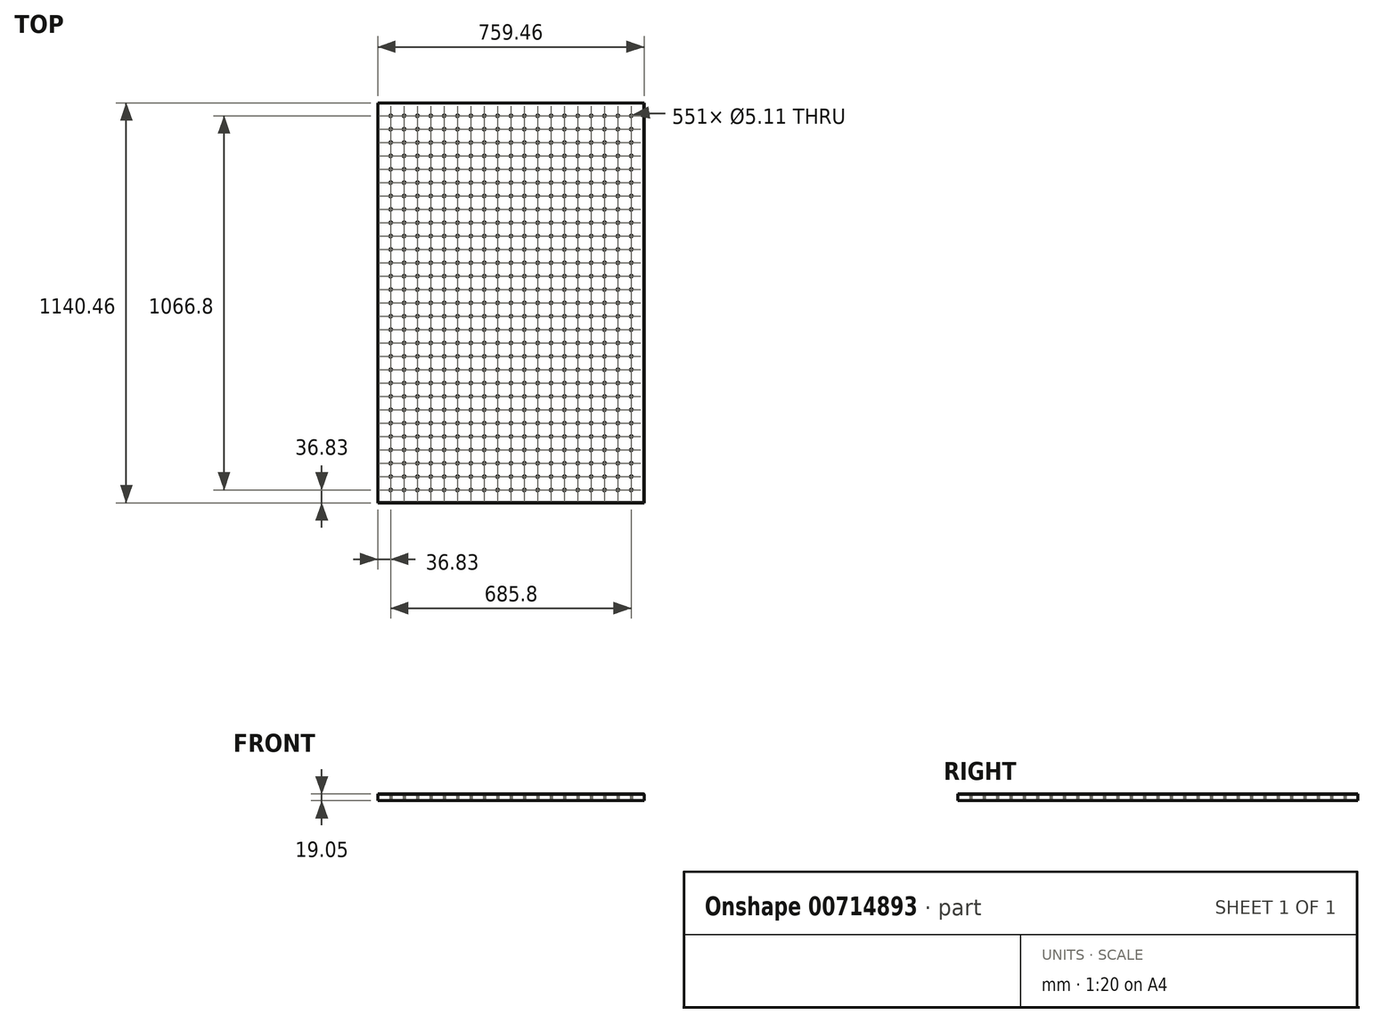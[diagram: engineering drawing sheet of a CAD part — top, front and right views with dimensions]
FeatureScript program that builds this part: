
annotation { "Feature Type Name" : "Feature", "Feature Type Description" : "" }
export const myFeature = defineFeature(function(context is Context, id is Id, definition is map)
    precondition{}
    {
        {
            var Q0;
            Q0=qCreatedBy(makeId("Top.planeOp"),FACE);
            var sketch = newSketch(context, id + "F0", { "sketchPlane" : qUnion([Q0])});
            skLineSegment(sketch, "E0.bottom", {"start": v(379.73, 570.23) * mm, "end": v(-379.73, 570.23) * mm});
            skLineSegment(sketch, "E0.top", {"start": v(379.73, -570.23) * mm, "end": v(-379.73, -570.23) * mm});
            skLineSegment(sketch, "E0.left", {"start": v(379.73, 570.23) * mm, "end": v(379.73, -570.23) * mm});
            skLineSegment(sketch, "E0.right", {"start": v(-379.73, 570.23) * mm, "end": v(-379.73, -570.23) * mm});
            skPoint(sketch, "E0.middle", {"position": v(0, 0) * mm});
            skLineSegment(sketch, "E1", {"start": v(0, 570.23) * mm, "end": v(0, -570.23) * mm, "construction": true});
            skCircle(sketch, "E2", {"center": v(0, 0) * mm, "radius": 2.55 * mm});
            skCircle(sketch, "E3.0.1.0", {"center": v(0, 38.1) * mm, "radius": 2.55 * mm});
            skCircle(sketch, "E3.0.2.0", {"center": v(0, 76.2) * mm, "radius": 2.55 * mm});
            skCircle(sketch, "E3.0.3.0", {"center": v(0, 114.3) * mm, "radius": 2.55 * mm});
            skCircle(sketch, "E3.0.4.0", {"center": v(0, 152.4) * mm, "radius": 2.55 * mm});
            skCircle(sketch, "E3.0.5.0", {"center": v(0, 190.5) * mm, "radius": 2.55 * mm});
            skCircle(sketch, "E3.0.6.0", {"center": v(0, 228.6) * mm, "radius": 2.55 * mm});
            skCircle(sketch, "E3.0.7.0", {"center": v(0, 266.7) * mm, "radius": 2.55 * mm});
            skCircle(sketch, "E3.0.8.0", {"center": v(0, 304.8) * mm, "radius": 2.55 * mm});
            skCircle(sketch, "E3.0.9.0", {"center": v(0, 342.9) * mm, "radius": 2.55 * mm});
            skCircle(sketch, "E3.0.10.0", {"center": v(0, 381) * mm, "radius": 2.55 * mm});
            skCircle(sketch, "E3.1.0.0", {"center": v(38.1, 0) * mm, "radius": 2.55 * mm});
            skCircle(sketch, "E3.1.1.0", {"center": v(38.1, 38.1) * mm, "radius": 2.55 * mm});
            skCircle(sketch, "E3.1.2.0", {"center": v(38.1, 76.2) * mm, "radius": 2.55 * mm});
            skCircle(sketch, "E3.1.3.0", {"center": v(38.1, 114.3) * mm, "radius": 2.55 * mm});
            skCircle(sketch, "E3.1.4.0", {"center": v(38.1, 152.4) * mm, "radius": 2.55 * mm});
            skCircle(sketch, "E3.1.5.0", {"center": v(38.1, 190.5) * mm, "radius": 2.55 * mm});
            skCircle(sketch, "E3.1.6.0", {"center": v(38.1, 228.6) * mm, "radius": 2.55 * mm});
            skCircle(sketch, "E3.1.7.0", {"center": v(38.1, 266.7) * mm, "radius": 2.55 * mm});
            skCircle(sketch, "E3.1.8.0", {"center": v(38.1, 304.8) * mm, "radius": 2.55 * mm});
            skCircle(sketch, "E3.1.9.0", {"center": v(38.1, 342.9) * mm, "radius": 2.55 * mm});
            skCircle(sketch, "E3.1.10.0", {"center": v(38.1, 381) * mm, "radius": 2.55 * mm});
            skCircle(sketch, "E3.2.0.0", {"center": v(76.2, 0) * mm, "radius": 2.55 * mm});
            skCircle(sketch, "E3.2.1.0", {"center": v(76.2, 38.1) * mm, "radius": 2.55 * mm});
            skCircle(sketch, "E3.2.2.0", {"center": v(76.2, 76.2) * mm, "radius": 2.55 * mm});
            skCircle(sketch, "E3.2.3.0", {"center": v(76.2, 114.3) * mm, "radius": 2.55 * mm});
            skCircle(sketch, "E3.2.4.0", {"center": v(76.2, 152.4) * mm, "radius": 2.55 * mm});
            skCircle(sketch, "E3.2.5.0", {"center": v(76.2, 190.5) * mm, "radius": 2.55 * mm});
            skCircle(sketch, "E3.2.6.0", {"center": v(76.2, 228.6) * mm, "radius": 2.55 * mm});
            skCircle(sketch, "E3.2.7.0", {"center": v(76.2, 266.7) * mm, "radius": 2.55 * mm});
            skCircle(sketch, "E3.2.8.0", {"center": v(76.2, 304.8) * mm, "radius": 2.55 * mm});
            skCircle(sketch, "E3.2.9.0", {"center": v(76.2, 342.9) * mm, "radius": 2.55 * mm});
            skCircle(sketch, "E3.2.10.0", {"center": v(76.2, 381) * mm, "radius": 2.55 * mm});
            skCircle(sketch, "E3.3.0.0", {"center": v(114.3, 0) * mm, "radius": 2.55 * mm});
            skCircle(sketch, "E3.3.1.0", {"center": v(114.3, 38.1) * mm, "radius": 2.55 * mm});
            skCircle(sketch, "E3.3.2.0", {"center": v(114.3, 76.2) * mm, "radius": 2.55 * mm});
            skCircle(sketch, "E3.3.3.0", {"center": v(114.3, 114.3) * mm, "radius": 2.55 * mm});
            skCircle(sketch, "E3.3.4.0", {"center": v(114.3, 152.4) * mm, "radius": 2.55 * mm});
            skCircle(sketch, "E3.3.5.0", {"center": v(114.3, 190.5) * mm, "radius": 2.55 * mm});
            skCircle(sketch, "E3.3.6.0", {"center": v(114.3, 228.6) * mm, "radius": 2.55 * mm});
            skCircle(sketch, "E3.3.7.0", {"center": v(114.3, 266.7) * mm, "radius": 2.55 * mm});
            skCircle(sketch, "E3.3.8.0", {"center": v(114.3, 304.8) * mm, "radius": 2.55 * mm});
            skCircle(sketch, "E3.3.9.0", {"center": v(114.3, 342.9) * mm, "radius": 2.55 * mm});
            skCircle(sketch, "E3.3.10.0", {"center": v(114.3, 381) * mm, "radius": 2.55 * mm});
            skCircle(sketch, "E3.4.0.0", {"center": v(152.4, 0) * mm, "radius": 2.55 * mm});
            skCircle(sketch, "E3.4.1.0", {"center": v(152.4, 38.1) * mm, "radius": 2.55 * mm});
            skCircle(sketch, "E3.4.2.0", {"center": v(152.4, 76.2) * mm, "radius": 2.55 * mm});
            skCircle(sketch, "E3.4.3.0", {"center": v(152.4, 114.3) * mm, "radius": 2.55 * mm});
            skCircle(sketch, "E3.4.4.0", {"center": v(152.4, 152.4) * mm, "radius": 2.55 * mm});
            skCircle(sketch, "E3.4.5.0", {"center": v(152.4, 190.5) * mm, "radius": 2.55 * mm});
            skCircle(sketch, "E3.4.6.0", {"center": v(152.4, 228.6) * mm, "radius": 2.55 * mm});
            skCircle(sketch, "E3.4.7.0", {"center": v(152.4, 266.7) * mm, "radius": 2.55 * mm});
            skCircle(sketch, "E3.4.8.0", {"center": v(152.4, 304.8) * mm, "radius": 2.55 * mm});
            skCircle(sketch, "E3.4.9.0", {"center": v(152.4, 342.9) * mm, "radius": 2.55 * mm});
            skCircle(sketch, "E3.4.10.0", {"center": v(152.4, 381) * mm, "radius": 2.55 * mm});
            skCircle(sketch, "E3.5.0.0", {"center": v(190.5, 0) * mm, "radius": 2.55 * mm});
            skCircle(sketch, "E3.5.1.0", {"center": v(190.5, 38.1) * mm, "radius": 2.55 * mm});
            skCircle(sketch, "E3.5.2.0", {"center": v(190.5, 76.2) * mm, "radius": 2.55 * mm});
            skCircle(sketch, "E3.5.3.0", {"center": v(190.5, 114.3) * mm, "radius": 2.55 * mm});
            skCircle(sketch, "E3.5.4.0", {"center": v(190.5, 152.4) * mm, "radius": 2.55 * mm});
            skCircle(sketch, "E3.5.5.0", {"center": v(190.5, 190.5) * mm, "radius": 2.55 * mm});
            skCircle(sketch, "E3.5.6.0", {"center": v(190.5, 228.6) * mm, "radius": 2.55 * mm});
            skCircle(sketch, "E3.5.7.0", {"center": v(190.5, 266.7) * mm, "radius": 2.55 * mm});
            skCircle(sketch, "E3.5.8.0", {"center": v(190.5, 304.8) * mm, "radius": 2.55 * mm});
            skCircle(sketch, "E3.5.9.0", {"center": v(190.5, 342.9) * mm, "radius": 2.55 * mm});
            skCircle(sketch, "E3.5.10.0", {"center": v(190.5, 381) * mm, "radius": 2.55 * mm});
            skCircle(sketch, "E3.6.0.0", {"center": v(228.6, 0) * mm, "radius": 2.55 * mm});
            skCircle(sketch, "E3.6.1.0", {"center": v(228.6, 38.1) * mm, "radius": 2.55 * mm});
            skCircle(sketch, "E3.6.2.0", {"center": v(228.6, 76.2) * mm, "radius": 2.55 * mm});
            skCircle(sketch, "E3.6.3.0", {"center": v(228.6, 114.3) * mm, "radius": 2.55 * mm});
            skCircle(sketch, "E3.6.4.0", {"center": v(228.6, 152.4) * mm, "radius": 2.55 * mm});
            skCircle(sketch, "E3.6.5.0", {"center": v(228.6, 190.5) * mm, "radius": 2.55 * mm});
            skCircle(sketch, "E3.6.6.0", {"center": v(228.6, 228.6) * mm, "radius": 2.55 * mm});
            skCircle(sketch, "E3.6.7.0", {"center": v(228.6, 266.7) * mm, "radius": 2.55 * mm});
            skCircle(sketch, "E3.6.8.0", {"center": v(228.6, 304.8) * mm, "radius": 2.55 * mm});
            skCircle(sketch, "E3.6.9.0", {"center": v(228.6, 342.9) * mm, "radius": 2.55 * mm});
            skCircle(sketch, "E3.6.10.0", {"center": v(228.6, 381) * mm, "radius": 2.55 * mm});
            skCircle(sketch, "E3.7.0.0", {"center": v(266.7, 0) * mm, "radius": 2.55 * mm});
            skCircle(sketch, "E3.7.1.0", {"center": v(266.7, 38.1) * mm, "radius": 2.55 * mm});
            skCircle(sketch, "E3.7.2.0", {"center": v(266.7, 76.2) * mm, "radius": 2.55 * mm});
            skCircle(sketch, "E3.7.3.0", {"center": v(266.7, 114.3) * mm, "radius": 2.55 * mm});
            skCircle(sketch, "E3.7.4.0", {"center": v(266.7, 152.4) * mm, "radius": 2.55 * mm});
            skCircle(sketch, "E3.7.5.0", {"center": v(266.7, 190.5) * mm, "radius": 2.55 * mm});
            skCircle(sketch, "E3.7.6.0", {"center": v(266.7, 228.6) * mm, "radius": 2.55 * mm});
            skCircle(sketch, "E3.7.7.0", {"center": v(266.7, 266.7) * mm, "radius": 2.55 * mm});
            skCircle(sketch, "E3.7.8.0", {"center": v(266.7, 304.8) * mm, "radius": 2.55 * mm});
            skCircle(sketch, "E3.7.9.0", {"center": v(266.7, 342.9) * mm, "radius": 2.55 * mm});
            skCircle(sketch, "E3.7.10.0", {"center": v(266.7, 381) * mm, "radius": 2.55 * mm});
            skLineSegment(sketch, "E3.direction1", {"start": v(0, 0) * mm, "end": v(38.1, 0) * mm, "construction": true});
            skLineSegment(sketch, "E3.direction2", {"start": v(0, 0) * mm, "end": v(0, 38.1) * mm, "construction": true});
            skCircle(sketch, "E4.0.0.11", {"center": v(0, 419.1) * mm, "radius": 2.55 * mm});
            skCircle(sketch, "E4.0.1.11", {"center": v(38.1, 419.1) * mm, "radius": 2.55 * mm});
            skCircle(sketch, "E4.0.2.11", {"center": v(76.2, 419.1) * mm, "radius": 2.55 * mm});
            skCircle(sketch, "E4.0.3.11", {"center": v(114.3, 419.1) * mm, "radius": 2.55 * mm});
            skCircle(sketch, "E4.0.4.11", {"center": v(152.4, 419.1) * mm, "radius": 2.55 * mm});
            skCircle(sketch, "E4.0.5.11", {"center": v(190.5, 419.1) * mm, "radius": 2.55 * mm});
            skCircle(sketch, "E4.0.6.11", {"center": v(228.6, 419.1) * mm, "radius": 2.55 * mm});
            skCircle(sketch, "E4.0.7.11", {"center": v(266.7, 419.1) * mm, "radius": 2.55 * mm});
            skCircle(sketch, "E5.0.0.12", {"center": v(0, 457.2) * mm, "radius": 2.55 * mm});
            skCircle(sketch, "E5.0.0.13", {"center": v(0, 495.3) * mm, "radius": 2.55 * mm});
            skCircle(sketch, "E5.0.0.14", {"center": v(0, 533.4) * mm, "radius": 2.55 * mm});
            skCircle(sketch, "E5.0.1.12", {"center": v(38.1, 457.2) * mm, "radius": 2.55 * mm});
            skCircle(sketch, "E5.0.1.13", {"center": v(38.1, 495.3) * mm, "radius": 2.55 * mm});
            skCircle(sketch, "E5.0.1.14", {"center": v(38.1, 533.4) * mm, "radius": 2.55 * mm});
            skCircle(sketch, "E5.0.2.12", {"center": v(76.2, 457.2) * mm, "radius": 2.55 * mm});
            skCircle(sketch, "E5.0.2.13", {"center": v(76.2, 495.3) * mm, "radius": 2.55 * mm});
            skCircle(sketch, "E5.0.2.14", {"center": v(76.2, 533.4) * mm, "radius": 2.55 * mm});
            skCircle(sketch, "E5.0.3.12", {"center": v(114.3, 457.2) * mm, "radius": 2.55 * mm});
            skCircle(sketch, "E5.0.3.13", {"center": v(114.3, 495.3) * mm, "radius": 2.55 * mm});
            skCircle(sketch, "E5.0.3.14", {"center": v(114.3, 533.4) * mm, "radius": 2.55 * mm});
            skCircle(sketch, "E5.0.4.12", {"center": v(152.4, 457.2) * mm, "radius": 2.55 * mm});
            skCircle(sketch, "E5.0.4.13", {"center": v(152.4, 495.3) * mm, "radius": 2.55 * mm});
            skCircle(sketch, "E5.0.4.14", {"center": v(152.4, 533.4) * mm, "radius": 2.55 * mm});
            skCircle(sketch, "E5.0.5.12", {"center": v(190.5, 457.2) * mm, "radius": 2.55 * mm});
            skCircle(sketch, "E5.0.5.13", {"center": v(190.5, 495.3) * mm, "radius": 2.55 * mm});
            skCircle(sketch, "E5.0.5.14", {"center": v(190.5, 533.4) * mm, "radius": 2.55 * mm});
            skCircle(sketch, "E5.0.6.12", {"center": v(228.6, 457.2) * mm, "radius": 2.55 * mm});
            skCircle(sketch, "E5.0.6.13", {"center": v(228.6, 495.3) * mm, "radius": 2.55 * mm});
            skCircle(sketch, "E5.0.6.14", {"center": v(228.6, 533.4) * mm, "radius": 2.55 * mm});
            skCircle(sketch, "E5.0.7.12", {"center": v(266.7, 457.2) * mm, "radius": 2.55 * mm});
            skCircle(sketch, "E5.0.7.13", {"center": v(266.7, 495.3) * mm, "radius": 2.55 * mm});
            skCircle(sketch, "E5.0.7.14", {"center": v(266.7, 533.4) * mm, "radius": 2.55 * mm});
            skCircle(sketch, "E6.0.8.0", {"center": v(304.8, 0) * mm, "radius": 2.55 * mm});
            skCircle(sketch, "E6.0.8.1", {"center": v(304.8, 38.1) * mm, "radius": 2.55 * mm});
            skCircle(sketch, "E6.0.8.2", {"center": v(304.8, 76.2) * mm, "radius": 2.55 * mm});
            skCircle(sketch, "E6.0.8.3", {"center": v(304.8, 114.3) * mm, "radius": 2.55 * mm});
            skCircle(sketch, "E6.0.8.4", {"center": v(304.8, 152.4) * mm, "radius": 2.55 * mm});
            skCircle(sketch, "E6.0.8.5", {"center": v(304.8, 190.5) * mm, "radius": 2.55 * mm});
            skCircle(sketch, "E6.0.8.6", {"center": v(304.8, 228.6) * mm, "radius": 2.55 * mm});
            skCircle(sketch, "E6.0.8.7", {"center": v(304.8, 266.7) * mm, "radius": 2.55 * mm});
            skCircle(sketch, "E6.0.8.8", {"center": v(304.8, 304.8) * mm, "radius": 2.55 * mm});
            skCircle(sketch, "E6.0.8.9", {"center": v(304.8, 342.9) * mm, "radius": 2.55 * mm});
            skCircle(sketch, "E6.0.8.10", {"center": v(304.8, 381) * mm, "radius": 2.55 * mm});
            skCircle(sketch, "E6.0.8.11", {"center": v(304.8, 419.1) * mm, "radius": 2.55 * mm});
            skCircle(sketch, "E6.0.8.12", {"center": v(304.8, 457.2) * mm, "radius": 2.55 * mm});
            skCircle(sketch, "E6.0.8.13", {"center": v(304.8, 495.3) * mm, "radius": 2.55 * mm});
            skCircle(sketch, "E6.0.8.14", {"center": v(304.8, 533.4) * mm, "radius": 2.55 * mm});
            skCircle(sketch, "E6.0.9.0", {"center": v(342.9, 0) * mm, "radius": 2.55 * mm});
            skCircle(sketch, "E6.0.9.1", {"center": v(342.9, 38.1) * mm, "radius": 2.55 * mm});
            skCircle(sketch, "E6.0.9.2", {"center": v(342.9, 76.2) * mm, "radius": 2.55 * mm});
            skCircle(sketch, "E6.0.9.3", {"center": v(342.9, 114.3) * mm, "radius": 2.55 * mm});
            skCircle(sketch, "E6.0.9.4", {"center": v(342.9, 152.4) * mm, "radius": 2.55 * mm});
            skCircle(sketch, "E6.0.9.5", {"center": v(342.9, 190.5) * mm, "radius": 2.55 * mm});
            skCircle(sketch, "E6.0.9.6", {"center": v(342.9, 228.6) * mm, "radius": 2.55 * mm});
            skCircle(sketch, "E6.0.9.7", {"center": v(342.9, 266.7) * mm, "radius": 2.55 * mm});
            skCircle(sketch, "E6.0.9.8", {"center": v(342.9, 304.8) * mm, "radius": 2.55 * mm});
            skCircle(sketch, "E6.0.9.9", {"center": v(342.9, 342.9) * mm, "radius": 2.55 * mm});
            skCircle(sketch, "E6.0.9.10", {"center": v(342.9, 381) * mm, "radius": 2.55 * mm});
            skCircle(sketch, "E6.0.9.11", {"center": v(342.9, 419.1) * mm, "radius": 2.55 * mm});
            skCircle(sketch, "E6.0.9.12", {"center": v(342.9, 457.2) * mm, "radius": 2.55 * mm});
            skCircle(sketch, "E6.0.9.13", {"center": v(342.9, 495.3) * mm, "radius": 2.55 * mm});
            skCircle(sketch, "E6.0.9.14", {"center": v(342.9, 533.4) * mm, "radius": 2.55 * mm});
            skLineSegment(sketch, "E7", {"start": v(-379.73, 0) * mm, "end": v(379.73, 0) * mm, "construction": true});
            skCircle(sketch, "E8.MirrorC", {"center": v(-228.6, 495.3) * mm, "radius": 2.55 * mm});
            skCircle(sketch, "E9.MirrorC", {"center": v(-76.2, 457.2) * mm, "radius": 2.55 * mm});
            skCircle(sketch, "E10.MirrorC", {"center": v(-266.7, 495.3) * mm, "radius": 2.55 * mm});
            skCircle(sketch, "E11.MirrorC", {"center": v(-114.3, 190.5) * mm, "radius": 2.55 * mm});
            skCircle(sketch, "E12.MirrorC", {"center": v(-304.8, 38.1) * mm, "radius": 2.55 * mm});
            skCircle(sketch, "E13.MirrorC", {"center": v(-114.3, 457.2) * mm, "radius": 2.55 * mm});
            skCircle(sketch, "E14.MirrorC", {"center": v(-266.7, 342.9) * mm, "radius": 2.55 * mm});
            skCircle(sketch, "E15.MirrorC", {"center": v(-304.8, 114.3) * mm, "radius": 2.55 * mm});
            skCircle(sketch, "E16.MirrorC", {"center": v(-76.2, 114.3) * mm, "radius": 2.55 * mm});
            skCircle(sketch, "E17.MirrorC", {"center": v(-190.5, 38.1) * mm, "radius": 2.55 * mm});
            skCircle(sketch, "E18.MirrorC", {"center": v(-190.5, 342.9) * mm, "radius": 2.55 * mm});
            skCircle(sketch, "E19.MirrorC", {"center": v(-266.7, 114.3) * mm, "radius": 2.55 * mm});
            skCircle(sketch, "E20.MirrorC", {"center": v(-266.7, 304.8) * mm, "radius": 2.55 * mm});
            skCircle(sketch, "E21.MirrorC", {"center": v(-190.5, 152.4) * mm, "radius": 2.55 * mm});
            skCircle(sketch, "E22.MirrorC", {"center": v(-38.1, 457.2) * mm, "radius": 2.55 * mm});
            skCircle(sketch, "E23.MirrorC", {"center": v(-228.6, 114.3) * mm, "radius": 2.55 * mm});
            skCircle(sketch, "E24.MirrorC", {"center": v(-342.9, 457.2) * mm, "radius": 2.55 * mm});
            skCircle(sketch, "E25.MirrorC", {"center": v(-76.2, 266.7) * mm, "radius": 2.55 * mm});
            skCircle(sketch, "E26.MirrorC", {"center": v(-228.6, 152.4) * mm, "radius": 2.55 * mm});
            skCircle(sketch, "E27.MirrorC", {"center": v(-38.1, 419.1) * mm, "radius": 2.55 * mm});
            skCircle(sketch, "E28.MirrorC", {"center": v(-38.1, 381) * mm, "radius": 2.55 * mm});
            skCircle(sketch, "E29.MirrorC", {"center": v(-114.3, 152.4) * mm, "radius": 2.55 * mm});
            skCircle(sketch, "E30.MirrorC", {"center": v(-228.6, 76.2) * mm, "radius": 2.55 * mm});
            skCircle(sketch, "E31.MirrorC", {"center": v(-266.7, 266.7) * mm, "radius": 2.55 * mm});
            skCircle(sketch, "E32.MirrorC", {"center": v(-38.1, 342.9) * mm, "radius": 2.55 * mm});
            skCircle(sketch, "E33.MirrorC", {"center": v(-152.4, 304.8) * mm, "radius": 2.55 * mm});
            skCircle(sketch, "E34.MirrorC", {"center": v(-342.9, 38.1) * mm, "radius": 2.55 * mm});
            skCircle(sketch, "E35.MirrorC", {"center": v(-114.3, 266.7) * mm, "radius": 2.55 * mm});
            skCircle(sketch, "E36.MirrorC", {"center": v(-76.2, 152.4) * mm, "radius": 2.55 * mm});
            skCircle(sketch, "E37.MirrorC", {"center": v(-228.6, 304.8) * mm, "radius": 2.55 * mm});
            skCircle(sketch, "E38.MirrorC", {"center": v(-38.1, 190.5) * mm, "radius": 2.55 * mm});
            skCircle(sketch, "E39.MirrorC", {"center": v(-114.3, 38.1) * mm, "radius": 2.55 * mm});
            skCircle(sketch, "E40.MirrorC", {"center": v(-152.4, 228.6) * mm, "radius": 2.55 * mm});
            skCircle(sketch, "E41.MirrorC", {"center": v(-266.7, 152.4) * mm, "radius": 2.55 * mm});
            skCircle(sketch, "E42.MirrorC", {"center": v(-266.7, 533.4) * mm, "radius": 2.55 * mm});
            skCircle(sketch, "E43.MirrorC", {"center": v(-228.6, 533.4) * mm, "radius": 2.55 * mm});
            skCircle(sketch, "E44.MirrorC", {"center": v(-76.2, 381) * mm, "radius": 2.55 * mm});
            skCircle(sketch, "E45.MirrorC", {"center": v(-114.3, 533.4) * mm, "radius": 2.55 * mm});
            skCircle(sketch, "E46.MirrorC", {"center": v(-114.3, 495.3) * mm, "radius": 2.55 * mm});
            skCircle(sketch, "E47.MirrorC", {"center": v(-342.9, 114.3) * mm, "radius": 2.55 * mm});
            skCircle(sketch, "E48.MirrorC", {"center": v(-152.4, 381) * mm, "radius": 2.55 * mm});
            skCircle(sketch, "E49.MirrorC", {"center": v(-228.6, 419.1) * mm, "radius": 2.55 * mm});
            skCircle(sketch, "E50.MirrorC", {"center": v(-304.8, 342.9) * mm, "radius": 2.55 * mm});
            skCircle(sketch, "E51.MirrorC", {"center": v(-114.3, 304.8) * mm, "radius": 2.55 * mm});
            skCircle(sketch, "E52.MirrorC", {"center": v(-342.9, 228.6) * mm, "radius": 2.55 * mm});
            skCircle(sketch, "E53.MirrorC", {"center": v(-76.2, 342.9) * mm, "radius": 2.55 * mm});
            skCircle(sketch, "E54.MirrorC", {"center": v(-342.9, 152.4) * mm, "radius": 2.55 * mm});
            skCircle(sketch, "E55.MirrorC", {"center": v(-190.5, 76.2) * mm, "radius": 2.55 * mm});
            skCircle(sketch, "E56.MirrorC", {"center": v(-228.6, 38.1) * mm, "radius": 2.55 * mm});
            skCircle(sketch, "E57.MirrorC", {"center": v(-152.4, 114.3) * mm, "radius": 2.55 * mm});
            skCircle(sketch, "E58.MirrorC", {"center": v(-38.1, 304.8) * mm, "radius": 2.55 * mm});
            skCircle(sketch, "E59.MirrorC", {"center": v(-152.4, 266.7) * mm, "radius": 2.55 * mm});
            skCircle(sketch, "E60.MirrorC", {"center": v(-190.5, 304.8) * mm, "radius": 2.55 * mm});
            skCircle(sketch, "E61.MirrorC", {"center": v(-266.7, 76.2) * mm, "radius": 2.55 * mm});
            skCircle(sketch, "E62.MirrorC", {"center": v(-114.3, 76.2) * mm, "radius": 2.55 * mm});
            skCircle(sketch, "E63.MirrorC", {"center": v(-304.8, 304.8) * mm, "radius": 2.55 * mm});
            skCircle(sketch, "E64.MirrorC", {"center": v(-304.8, 533.4) * mm, "radius": 2.55 * mm});
            skCircle(sketch, "E65.MirrorC", {"center": v(-190.5, 114.3) * mm, "radius": 2.55 * mm});
            skCircle(sketch, "E66.MirrorC", {"center": v(-76.2, 76.2) * mm, "radius": 2.55 * mm});
            skCircle(sketch, "E67.MirrorC", {"center": v(-266.7, 190.5) * mm, "radius": 2.55 * mm});
            skCircle(sketch, "E68.MirrorC", {"center": v(-152.4, 38.1) * mm, "radius": 2.55 * mm});
            skCircle(sketch, "E69.MirrorC", {"center": v(-190.5, 228.6) * mm, "radius": 2.55 * mm});
            skCircle(sketch, "E70.MirrorC", {"center": v(-190.5, 495.3) * mm, "radius": 2.55 * mm});
            skCircle(sketch, "E71.MirrorC", {"center": v(-38.1, 266.7) * mm, "radius": 2.55 * mm});
            skCircle(sketch, "E72.MirrorC", {"center": v(-152.4, 495.3) * mm, "radius": 2.55 * mm});
            skCircle(sketch, "E73.MirrorC", {"center": v(-38.1, 152.4) * mm, "radius": 2.55 * mm});
            skCircle(sketch, "E74.MirrorC", {"center": v(-304.8, 495.3) * mm, "radius": 2.55 * mm});
            skCircle(sketch, "E75.MirrorC", {"center": v(-304.8, 381) * mm, "radius": 2.55 * mm});
            skCircle(sketch, "E76.MirrorC", {"center": v(-228.6, 190.5) * mm, "radius": 2.55 * mm});
            skCircle(sketch, "E77.MirrorC", {"center": v(-38.1, 76.2) * mm, "radius": 2.55 * mm});
            skCircle(sketch, "E78.MirrorC", {"center": v(-342.9, 76.2) * mm, "radius": 2.55 * mm});
            skCircle(sketch, "E79.MirrorC", {"center": v(-266.7, 419.1) * mm, "radius": 2.55 * mm});
            skCircle(sketch, "E80.MirrorC", {"center": v(-190.5, 190.5) * mm, "radius": 2.55 * mm});
            skCircle(sketch, "E81.MirrorC", {"center": v(-152.4, 419.1) * mm, "radius": 2.55 * mm});
            skCircle(sketch, "E82.MirrorC", {"center": v(-38.1, 533.4) * mm, "radius": 2.55 * mm});
            skCircle(sketch, "E83.MirrorC", {"center": v(-76.2, 228.6) * mm, "radius": 2.55 * mm});
            skCircle(sketch, "E84.MirrorC", {"center": v(-114.3, 342.9) * mm, "radius": 2.55 * mm});
            skCircle(sketch, "E85.MirrorC", {"center": v(-228.6, 266.7) * mm, "radius": 2.55 * mm});
            skCircle(sketch, "E86.MirrorC", {"center": v(-304.8, 419.1) * mm, "radius": 2.55 * mm});
            skCircle(sketch, "E87.MirrorC", {"center": v(-38.1, 495.3) * mm, "radius": 2.55 * mm});
            skCircle(sketch, "E88.MirrorC", {"center": v(-190.5, 381) * mm, "radius": 2.55 * mm});
            skCircle(sketch, "E89.MirrorC", {"center": v(-304.8, 76.2) * mm, "radius": 2.55 * mm});
            skCircle(sketch, "E90.MirrorC", {"center": v(-190.5, 457.2) * mm, "radius": 2.55 * mm});
            skCircle(sketch, "E91.MirrorC", {"center": v(-76.2, 419.1) * mm, "radius": 2.55 * mm});
            skCircle(sketch, "E92.MirrorC", {"center": v(-342.9, 266.7) * mm, "radius": 2.55 * mm});
            skCircle(sketch, "E93.MirrorC", {"center": v(-190.5, 533.4) * mm, "radius": 2.55 * mm});
            skCircle(sketch, "E94.MirrorC", {"center": v(-266.7, 228.6) * mm, "radius": 2.55 * mm});
            skCircle(sketch, "E95.MirrorC", {"center": v(-342.9, 381) * mm, "radius": 2.55 * mm});
            skCircle(sketch, "E96.MirrorC", {"center": v(-38.1, 38.1) * mm, "radius": 2.55 * mm});
            skCircle(sketch, "E97.MirrorC", {"center": v(-114.3, 228.6) * mm, "radius": 2.55 * mm});
            skCircle(sketch, "E98.MirrorC", {"center": v(-38.1, 228.6) * mm, "radius": 2.55 * mm});
            skCircle(sketch, "E99.MirrorC", {"center": v(-304.8, 190.5) * mm, "radius": 2.55 * mm});
            skCircle(sketch, "E100.MirrorC", {"center": v(-114.3, 114.3) * mm, "radius": 2.55 * mm});
            skCircle(sketch, "E101.MirrorC", {"center": v(-228.6, 457.2) * mm, "radius": 2.55 * mm});
            skCircle(sketch, "E102.MirrorC", {"center": v(-342.9, 419.1) * mm, "radius": 2.55 * mm});
            skCircle(sketch, "E103.MirrorC", {"center": v(-266.7, 381) * mm, "radius": 2.55 * mm});
            skCircle(sketch, "E104.MirrorC", {"center": v(-342.9, 533.4) * mm, "radius": 2.55 * mm});
            skCircle(sketch, "E105.MirrorC", {"center": v(-114.3, 381) * mm, "radius": 2.55 * mm});
            skCircle(sketch, "E106.MirrorC", {"center": v(-342.9, 495.3) * mm, "radius": 2.55 * mm});
            skCircle(sketch, "E107.MirrorC", {"center": v(-266.7, 457.2) * mm, "radius": 2.55 * mm});
            skCircle(sketch, "E108.MirrorC", {"center": v(-342.9, 304.8) * mm, "radius": 2.55 * mm});
            skCircle(sketch, "E109.MirrorC", {"center": v(-152.4, 190.5) * mm, "radius": 2.55 * mm});
            skCircle(sketch, "E110.MirrorC", {"center": v(-114.3, 419.1) * mm, "radius": 2.55 * mm});
            skCircle(sketch, "E111.MirrorC", {"center": v(-228.6, 342.9) * mm, "radius": 2.55 * mm});
            skCircle(sketch, "E112.MirrorC", {"center": v(-76.2, 190.5) * mm, "radius": 2.55 * mm});
            skCircle(sketch, "E113.MirrorC", {"center": v(-152.4, 152.4) * mm, "radius": 2.55 * mm});
            skCircle(sketch, "E114.MirrorC", {"center": v(-304.8, 457.2) * mm, "radius": 2.55 * mm});
            skCircle(sketch, "E115.MirrorC", {"center": v(-76.2, 533.4) * mm, "radius": 2.55 * mm});
            skCircle(sketch, "E116.MirrorC", {"center": v(-228.6, 228.6) * mm, "radius": 2.55 * mm});
            skCircle(sketch, "E117.MirrorC", {"center": v(-76.2, 495.3) * mm, "radius": 2.55 * mm});
            skCircle(sketch, "E118.MirrorC", {"center": v(-38.1, 114.3) * mm, "radius": 2.55 * mm});
            skCircle(sketch, "E119.MirrorC", {"center": v(-266.7, 38.1) * mm, "radius": 2.55 * mm});
            skCircle(sketch, "E120.MirrorC", {"center": v(-190.5, 266.7) * mm, "radius": 2.55 * mm});
            skCircle(sketch, "E121.MirrorC", {"center": v(-152.4, 342.9) * mm, "radius": 2.55 * mm});
            skCircle(sketch, "E122.MirrorC", {"center": v(-76.2, 304.8) * mm, "radius": 2.55 * mm});
            skCircle(sketch, "E123.MirrorC", {"center": v(-304.8, 266.7) * mm, "radius": 2.55 * mm});
            skCircle(sketch, "E124.MirrorC", {"center": v(-190.5, 419.1) * mm, "radius": 2.55 * mm});
            skCircle(sketch, "E125.MirrorC", {"center": v(-152.4, 76.2) * mm, "radius": 2.55 * mm});
            skCircle(sketch, "E126.MirrorC", {"center": v(-304.8, 228.6) * mm, "radius": 2.55 * mm});
            skCircle(sketch, "E127.MirrorC", {"center": v(-342.9, 342.9) * mm, "radius": 2.55 * mm});
            skCircle(sketch, "E128.MirrorC", {"center": v(-152.4, 533.4) * mm, "radius": 2.55 * mm});
            skCircle(sketch, "E129.MirrorC", {"center": v(-342.9, 190.5) * mm, "radius": 2.55 * mm});
            skCircle(sketch, "E130.MirrorC", {"center": v(-76.2, 38.1) * mm, "radius": 2.55 * mm});
            skCircle(sketch, "E131.MirrorC", {"center": v(-228.6, 381) * mm, "radius": 2.55 * mm});
            skCircle(sketch, "E132.MirrorC", {"center": v(-304.8, 152.4) * mm, "radius": 2.55 * mm});
            skCircle(sketch, "E133.MirrorC", {"center": v(-152.4, 457.2) * mm, "radius": 2.55 * mm});
            skLineSegment(sketch, "E134.MirrorCS", {"start": v(0, 0) * mm, "end": v(-38.1, 0) * mm, "construction": true});
            skCircle(sketch, "E135.MirrorC", {"center": v(-38.1, 0) * mm, "radius": 2.55 * mm});
            skCircle(sketch, "E136.MirrorC", {"center": v(-114.3, 0) * mm, "radius": 2.55 * mm});
            skCircle(sketch, "E137.MirrorC", {"center": v(-228.6, 0) * mm, "radius": 2.55 * mm});
            skCircle(sketch, "E138.MirrorC", {"center": v(-266.7, 0) * mm, "radius": 2.55 * mm});
            skCircle(sketch, "E139.MirrorC", {"center": v(-152.4, 0) * mm, "radius": 2.55 * mm});
            skCircle(sketch, "E140.MirrorC", {"center": v(-304.8, 0) * mm, "radius": 2.55 * mm});
            skCircle(sketch, "E141.MirrorC", {"center": v(-342.9, 0) * mm, "radius": 2.55 * mm});
            skCircle(sketch, "E142.MirrorC", {"center": v(-76.2, 0) * mm, "radius": 2.55 * mm});
            skCircle(sketch, "E143.MirrorC", {"center": v(-190.5, 0) * mm, "radius": 2.55 * mm});
            skLineSegment(sketch, "E144.MirrorCS", {"start": v(379.73, 0) * mm, "end": v(-379.73, 0) * mm, "construction": true});
            skCircle(sketch, "E145.MirrorC", {"center": v(0, -38.1) * mm, "radius": 2.55 * mm});
            skCircle(sketch, "E146.MirrorC", {"center": v(0, -114.3) * mm, "radius": 2.55 * mm});
            skCircle(sketch, "E147.MirrorC", {"center": v(0, -495.3) * mm, "radius": 2.55 * mm});
            skCircle(sketch, "E148.MirrorC", {"center": v(0, -457.2) * mm, "radius": 2.55 * mm});
            skCircle(sketch, "E149.MirrorC", {"center": v(0, -533.4) * mm, "radius": 2.55 * mm});
            skCircle(sketch, "E150.MirrorC", {"center": v(0, -304.8) * mm, "radius": 2.55 * mm});
            skCircle(sketch, "E151.MirrorC", {"center": v(0, -228.6) * mm, "radius": 2.55 * mm});
            skCircle(sketch, "E152.MirrorC", {"center": v(0, -381) * mm, "radius": 2.55 * mm});
            skCircle(sketch, "E153.MirrorC", {"center": v(0, -419.1) * mm, "radius": 2.55 * mm});
            skCircle(sketch, "E154.MirrorC", {"center": v(0, -190.5) * mm, "radius": 2.55 * mm});
            skCircle(sketch, "E155.MirrorC", {"center": v(0, -152.4) * mm, "radius": 2.55 * mm});
            skCircle(sketch, "E156.MirrorC", {"center": v(0, -342.9) * mm, "radius": 2.55 * mm});
            skCircle(sketch, "E157.MirrorC", {"center": v(0, -76.2) * mm, "radius": 2.55 * mm});
            skCircle(sketch, "E158.MirrorC", {"center": v(0, -266.7) * mm, "radius": 2.55 * mm});
            skCircle(sketch, "E159.MirrorC", {"center": v(-38.1, -495.3) * mm, "radius": 2.55 * mm});
            skCircle(sketch, "E160.MirrorC", {"center": v(-114.3, -228.6) * mm, "radius": 2.55 * mm});
            skCircle(sketch, "E161.MirrorC", {"center": v(-152.4, -495.3) * mm, "radius": 2.55 * mm});
            skCircle(sketch, "E162.MirrorC", {"center": v(114.3, -457.2) * mm, "radius": 2.55 * mm});
            skCircle(sketch, "E163.MirrorC", {"center": v(-38.1, -114.3) * mm, "radius": 2.55 * mm});
            skCircle(sketch, "E164.MirrorC", {"center": v(-266.7, -342.9) * mm, "radius": 2.55 * mm});
            skCircle(sketch, "E165.MirrorC", {"center": v(-266.7, -533.4) * mm, "radius": 2.55 * mm});
            skCircle(sketch, "E166.MirrorC", {"center": v(-38.1, -266.7) * mm, "radius": 2.55 * mm});
            skCircle(sketch, "E167.MirrorC", {"center": v(-114.3, -114.3) * mm, "radius": 2.55 * mm});
            skCircle(sketch, "E168.MirrorC", {"center": v(38.1, -228.6) * mm, "radius": 2.55 * mm});
            skCircle(sketch, "E169.MirrorC", {"center": v(-76.2, -76.2) * mm, "radius": 2.55 * mm});
            skCircle(sketch, "E170.MirrorC", {"center": v(-190.5, -190.5) * mm, "radius": 2.55 * mm});
            skCircle(sketch, "E171.MirrorC", {"center": v(-152.4, -533.4) * mm, "radius": 2.55 * mm});
            skCircle(sketch, "E172.MirrorC", {"center": v(304.8, -228.6) * mm, "radius": 2.55 * mm});
            skCircle(sketch, "E173.MirrorC", {"center": v(152.4, -495.3) * mm, "radius": 2.55 * mm});
            skCircle(sketch, "E174.MirrorC", {"center": v(304.8, -190.5) * mm, "radius": 2.55 * mm});
            skCircle(sketch, "E175.MirrorC", {"center": v(342.9, -228.6) * mm, "radius": 2.55 * mm});
            skCircle(sketch, "E176.MirrorC", {"center": v(304.8, -266.7) * mm, "radius": 2.55 * mm});
            skCircle(sketch, "E177.MirrorC", {"center": v(-228.6, -495.3) * mm, "radius": 2.55 * mm});
            skCircle(sketch, "E178.MirrorC", {"center": v(190.5, -533.4) * mm, "radius": 2.55 * mm});
            skCircle(sketch, "E179.MirrorC", {"center": v(266.7, -228.6) * mm, "radius": 2.55 * mm});
            skCircle(sketch, "E180.MirrorC", {"center": v(228.6, -38.1) * mm, "radius": 2.55 * mm});
            skCircle(sketch, "E181.MirrorC", {"center": v(-152.4, -304.8) * mm, "radius": 2.55 * mm});
            skCircle(sketch, "E182.MirrorC", {"center": v(-190.5, -38.1) * mm, "radius": 2.55 * mm});
            skCircle(sketch, "E183.MirrorC", {"center": v(342.9, -381) * mm, "radius": 2.55 * mm});
            skCircle(sketch, "E184.MirrorC", {"center": v(190.5, -304.8) * mm, "radius": 2.55 * mm});
            skCircle(sketch, "E185.MirrorC", {"center": v(304.8, -342.9) * mm, "radius": 2.55 * mm});
            skCircle(sketch, "E186.MirrorC", {"center": v(266.7, -114.3) * mm, "radius": 2.55 * mm});
            skCircle(sketch, "E187.MirrorC", {"center": v(-190.5, -228.6) * mm, "radius": 2.55 * mm});
            skCircle(sketch, "E188.MirrorC", {"center": v(-152.4, -190.5) * mm, "radius": 2.55 * mm});
            skCircle(sketch, "E189.MirrorC", {"center": v(-304.8, -342.9) * mm, "radius": 2.55 * mm});
            skCircle(sketch, "E190.MirrorC", {"center": v(-304.8, -76.2) * mm, "radius": 2.55 * mm});
            skCircle(sketch, "E191.MirrorC", {"center": v(-304.8, -495.3) * mm, "radius": 2.55 * mm});
            skCircle(sketch, "E192.MirrorC", {"center": v(342.9, -304.8) * mm, "radius": 2.55 * mm});
            skCircle(sketch, "E193.MirrorC", {"center": v(-76.2, -495.3) * mm, "radius": 2.55 * mm});
            skCircle(sketch, "E194.MirrorC", {"center": v(-228.6, -76.2) * mm, "radius": 2.55 * mm});
            skCircle(sketch, "E195.MirrorC", {"center": v(-190.5, -266.7) * mm, "radius": 2.55 * mm});
            skCircle(sketch, "E196.MirrorC", {"center": v(-38.1, -457.2) * mm, "radius": 2.55 * mm});
            skCircle(sketch, "E197.MirrorC", {"center": v(304.8, -533.4) * mm, "radius": 2.55 * mm});
            skCircle(sketch, "E198.MirrorC", {"center": v(-76.2, -228.6) * mm, "radius": 2.55 * mm});
            skCircle(sketch, "E199.MirrorC", {"center": v(-342.9, -495.3) * mm, "radius": 2.55 * mm});
            skCircle(sketch, "E200.MirrorC", {"center": v(-76.2, -304.8) * mm, "radius": 2.55 * mm});
            skCircle(sketch, "E201.MirrorC", {"center": v(-342.9, -76.2) * mm, "radius": 2.55 * mm});
            skCircle(sketch, "E202.MirrorC", {"center": v(-342.9, -114.3) * mm, "radius": 2.55 * mm});
            skCircle(sketch, "E203.MirrorC", {"center": v(-304.8, -533.4) * mm, "radius": 2.55 * mm});
            skCircle(sketch, "E204.MirrorC", {"center": v(342.9, -495.3) * mm, "radius": 2.55 * mm});
            skCircle(sketch, "E205.MirrorC", {"center": v(-266.7, -304.8) * mm, "radius": 2.55 * mm});
            skCircle(sketch, "E206.MirrorC", {"center": v(-228.6, -419.1) * mm, "radius": 2.55 * mm});
            skCircle(sketch, "E207.MirrorC", {"center": v(266.7, -342.9) * mm, "radius": 2.55 * mm});
            skCircle(sketch, "E208.MirrorC", {"center": v(-114.3, -266.7) * mm, "radius": 2.55 * mm});
            skCircle(sketch, "E209.MirrorC", {"center": v(76.2, -457.2) * mm, "radius": 2.55 * mm});
            skCircle(sketch, "E210.MirrorC", {"center": v(38.1, -495.3) * mm, "radius": 2.55 * mm});
            skCircle(sketch, "E211.MirrorC", {"center": v(266.7, -533.4) * mm, "radius": 2.55 * mm});
            skCircle(sketch, "E212.MirrorC", {"center": v(38.1, -76.2) * mm, "radius": 2.55 * mm});
            skCircle(sketch, "E213.MirrorC", {"center": v(76.2, -266.7) * mm, "radius": 2.55 * mm});
            skCircle(sketch, "E214.MirrorC", {"center": v(152.4, -76.2) * mm, "radius": 2.55 * mm});
            skCircle(sketch, "E215.MirrorC", {"center": v(152.4, -266.7) * mm, "radius": 2.55 * mm});
            skCircle(sketch, "E216.MirrorC", {"center": v(-114.3, -190.5) * mm, "radius": 2.55 * mm});
            skCircle(sketch, "E217.MirrorC", {"center": v(342.9, -190.5) * mm, "radius": 2.55 * mm});
            skCircle(sketch, "E218.MirrorC", {"center": v(38.1, -381) * mm, "radius": 2.55 * mm});
            skCircle(sketch, "E219.MirrorC", {"center": v(-228.6, -114.3) * mm, "radius": 2.55 * mm});
            skCircle(sketch, "E220.MirrorC", {"center": v(38.1, -304.8) * mm, "radius": 2.55 * mm});
            skCircle(sketch, "E221.MirrorC", {"center": v(-114.3, -304.8) * mm, "radius": 2.55 * mm});
            skCircle(sketch, "E222.MirrorC", {"center": v(-342.9, -381) * mm, "radius": 2.55 * mm});
            skCircle(sketch, "E223.MirrorC", {"center": v(114.3, -76.2) * mm, "radius": 2.55 * mm});
            skCircle(sketch, "E224.MirrorC", {"center": v(-304.8, -38.1) * mm, "radius": 2.55 * mm});
            skCircle(sketch, "E225.MirrorC", {"center": v(342.9, -76.2) * mm, "radius": 2.55 * mm});
            skCircle(sketch, "E226.MirrorC", {"center": v(-38.1, -38.1) * mm, "radius": 2.55 * mm});
            skCircle(sketch, "E227.MirrorC", {"center": v(266.7, -38.1) * mm, "radius": 2.55 * mm});
            skCircle(sketch, "E228.MirrorC", {"center": v(190.5, -266.7) * mm, "radius": 2.55 * mm});
            skCircle(sketch, "E229.MirrorC", {"center": v(76.2, -304.8) * mm, "radius": 2.55 * mm});
            skCircle(sketch, "E230.MirrorC", {"center": v(152.4, -228.6) * mm, "radius": 2.55 * mm});
            skCircle(sketch, "E231.MirrorC", {"center": v(-114.3, -152.4) * mm, "radius": 2.55 * mm});
            skCircle(sketch, "E232.MirrorC", {"center": v(-114.3, -457.2) * mm, "radius": 2.55 * mm});
            skCircle(sketch, "E233.MirrorC", {"center": v(342.9, -152.4) * mm, "radius": 2.55 * mm});
            skCircle(sketch, "E234.MirrorC", {"center": v(228.6, -533.4) * mm, "radius": 2.55 * mm});
            skCircle(sketch, "E235.MirrorC", {"center": v(-190.5, -419.1) * mm, "radius": 2.55 * mm});
            skCircle(sketch, "E236.MirrorC", {"center": v(342.9, -114.3) * mm, "radius": 2.55 * mm});
            skCircle(sketch, "E237.MirrorC", {"center": v(304.8, -76.2) * mm, "radius": 2.55 * mm});
            skCircle(sketch, "E238.MirrorC", {"center": v(76.2, -419.1) * mm, "radius": 2.55 * mm});
            skCircle(sketch, "E239.MirrorC", {"center": v(304.8, -38.1) * mm, "radius": 2.55 * mm});
            skCircle(sketch, "E240.MirrorC", {"center": v(38.1, -419.1) * mm, "radius": 2.55 * mm});
            skCircle(sketch, "E241.MirrorC", {"center": v(304.8, -114.3) * mm, "radius": 2.55 * mm});
            skCircle(sketch, "E242.MirrorC", {"center": v(-76.2, -533.4) * mm, "radius": 2.55 * mm});
            skCircle(sketch, "E243.MirrorC", {"center": v(-342.9, -342.9) * mm, "radius": 2.55 * mm});
            skCircle(sketch, "E244.MirrorC", {"center": v(266.7, -152.4) * mm, "radius": 2.55 * mm});
            skCircle(sketch, "E245.MirrorC", {"center": v(-190.5, -76.2) * mm, "radius": 2.55 * mm});
            skCircle(sketch, "E246.MirrorC", {"center": v(114.3, -190.5) * mm, "radius": 2.55 * mm});
            skCircle(sketch, "E247.MirrorC", {"center": v(152.4, -381) * mm, "radius": 2.55 * mm});
            skCircle(sketch, "E248.MirrorC", {"center": v(38.1, -266.7) * mm, "radius": 2.55 * mm});
            skCircle(sketch, "E249.MirrorC", {"center": v(-228.6, -266.7) * mm, "radius": 2.55 * mm});
            skCircle(sketch, "E250.MirrorC", {"center": v(114.3, -419.1) * mm, "radius": 2.55 * mm});
            skCircle(sketch, "E251.MirrorC", {"center": v(190.5, -381) * mm, "radius": 2.55 * mm});
            skCircle(sketch, "E252.MirrorC", {"center": v(-228.6, -304.8) * mm, "radius": 2.55 * mm});
            skCircle(sketch, "E253.MirrorC", {"center": v(190.5, -495.3) * mm, "radius": 2.55 * mm});
            skCircle(sketch, "E254.MirrorC", {"center": v(228.6, -266.7) * mm, "radius": 2.55 * mm});
            skCircle(sketch, "E255.MirrorC", {"center": v(38.1, -114.3) * mm, "radius": 2.55 * mm});
            skCircle(sketch, "E256.MirrorC", {"center": v(-342.9, -190.5) * mm, "radius": 2.55 * mm});
            skCircle(sketch, "E257.MirrorC", {"center": v(-342.9, -457.2) * mm, "radius": 2.55 * mm});
            skCircle(sketch, "E258.MirrorC", {"center": v(-38.1, -152.4) * mm, "radius": 2.55 * mm});
            skCircle(sketch, "E259.MirrorC", {"center": v(38.1, -457.2) * mm, "radius": 2.55 * mm});
            skCircle(sketch, "E260.MirrorC", {"center": v(266.7, -304.8) * mm, "radius": 2.55 * mm});
            skCircle(sketch, "E261.MirrorC", {"center": v(228.6, -114.3) * mm, "radius": 2.55 * mm});
            skCircle(sketch, "E262.MirrorC", {"center": v(-76.2, -38.1) * mm, "radius": 2.55 * mm});
            skCircle(sketch, "E263.MirrorC", {"center": v(-228.6, -342.9) * mm, "radius": 2.55 * mm});
            skCircle(sketch, "E264.MirrorC", {"center": v(266.7, -190.5) * mm, "radius": 2.55 * mm});
            skCircle(sketch, "E265.MirrorC", {"center": v(152.4, -38.1) * mm, "radius": 2.55 * mm});
            skCircle(sketch, "E266.MirrorC", {"center": v(190.5, -228.6) * mm, "radius": 2.55 * mm});
            skCircle(sketch, "E267.MirrorC", {"center": v(-38.1, -304.8) * mm, "radius": 2.55 * mm});
            skCircle(sketch, "E268.MirrorC", {"center": v(-76.2, -114.3) * mm, "radius": 2.55 * mm});
            skCircle(sketch, "E269.MirrorC", {"center": v(-266.7, -495.3) * mm, "radius": 2.55 * mm});
            skCircle(sketch, "E270.MirrorC", {"center": v(-38.1, -190.5) * mm, "radius": 2.55 * mm});
            skCircle(sketch, "E271.MirrorC", {"center": v(-76.2, -419.1) * mm, "radius": 2.55 * mm});
            skCircle(sketch, "E272.MirrorC", {"center": v(-266.7, -76.2) * mm, "radius": 2.55 * mm});
            skCircle(sketch, "E273.MirrorC", {"center": v(-76.2, -342.9) * mm, "radius": 2.55 * mm});
            skCircle(sketch, "E274.MirrorC", {"center": v(-38.1, -533.4) * mm, "radius": 2.55 * mm});
            skCircle(sketch, "E275.MirrorC", {"center": v(-114.3, -495.3) * mm, "radius": 2.55 * mm});
            skCircle(sketch, "E276.MirrorC", {"center": v(-342.9, -304.8) * mm, "radius": 2.55 * mm});
            skCircle(sketch, "E277.MirrorC", {"center": v(-342.9, -533.4) * mm, "radius": 2.55 * mm});
            skCircle(sketch, "E278.MirrorC", {"center": v(-114.3, -419.1) * mm, "radius": 2.55 * mm});
            skCircle(sketch, "E279.MirrorC", {"center": v(-266.7, -228.6) * mm, "radius": 2.55 * mm});
            skCircle(sketch, "E280.MirrorC", {"center": v(-228.6, -228.6) * mm, "radius": 2.55 * mm});
            skCircle(sketch, "E281.MirrorC", {"center": v(-342.9, -152.4) * mm, "radius": 2.55 * mm});
            skCircle(sketch, "E282.MirrorC", {"center": v(-152.4, -266.7) * mm, "radius": 2.55 * mm});
            skCircle(sketch, "E283.MirrorC", {"center": v(76.2, -190.5) * mm, "radius": 2.55 * mm});
            skCircle(sketch, "E284.MirrorC", {"center": v(-76.2, -381) * mm, "radius": 2.55 * mm});
            skCircle(sketch, "E285.MirrorC", {"center": v(-304.8, -152.4) * mm, "radius": 2.55 * mm});
            skCircle(sketch, "E286.MirrorC", {"center": v(-266.7, -38.1) * mm, "radius": 2.55 * mm});
            skCircle(sketch, "E287.MirrorC", {"center": v(-266.7, -381) * mm, "radius": 2.55 * mm});
            skCircle(sketch, "E288.MirrorC", {"center": v(152.4, -190.5) * mm, "radius": 2.55 * mm});
            skCircle(sketch, "E289.MirrorC", {"center": v(-76.2, -152.4) * mm, "radius": 2.55 * mm});
            skCircle(sketch, "E290.MirrorC", {"center": v(266.7, -495.3) * mm, "radius": 2.55 * mm});
            skCircle(sketch, "E291.MirrorC", {"center": v(152.4, -304.8) * mm, "radius": 2.55 * mm});
            skCircle(sketch, "E292.MirrorC", {"center": v(-266.7, -190.5) * mm, "radius": 2.55 * mm});
            skCircle(sketch, "E293.MirrorC", {"center": v(-152.4, -419.1) * mm, "radius": 2.55 * mm});
            skCircle(sketch, "E294.MirrorC", {"center": v(76.2, -114.3) * mm, "radius": 2.55 * mm});
            skCircle(sketch, "E295.MirrorC", {"center": v(-342.9, -228.6) * mm, "radius": 2.55 * mm});
            skCircle(sketch, "E296.MirrorC", {"center": v(114.3, -114.3) * mm, "radius": 2.55 * mm});
            skCircle(sketch, "E297.MirrorC", {"center": v(38.1, -342.9) * mm, "radius": 2.55 * mm});
            skCircle(sketch, "E298.MirrorC", {"center": v(-228.6, -190.5) * mm, "radius": 2.55 * mm});
            skCircle(sketch, "E299.MirrorC", {"center": v(228.6, -457.2) * mm, "radius": 2.55 * mm});
            skCircle(sketch, "E300.MirrorC", {"center": v(266.7, -266.7) * mm, "radius": 2.55 * mm});
            skCircle(sketch, "E301.MirrorC", {"center": v(228.6, -76.2) * mm, "radius": 2.55 * mm});
            skCircle(sketch, "E302.MirrorC", {"center": v(114.3, -495.3) * mm, "radius": 2.55 * mm});
            skCircle(sketch, "E303.MirrorC", {"center": v(76.2, -228.6) * mm, "radius": 2.55 * mm});
            skCircle(sketch, "E304.MirrorC", {"center": v(-304.8, -419.1) * mm, "radius": 2.55 * mm});
            skCircle(sketch, "E305.MirrorC", {"center": v(304.8, -419.1) * mm, "radius": 2.55 * mm});
            skCircle(sketch, "E306.MirrorC", {"center": v(-152.4, -228.6) * mm, "radius": 2.55 * mm});
            skCircle(sketch, "E307.MirrorC", {"center": v(-228.6, -381) * mm, "radius": 2.55 * mm});
            skCircle(sketch, "E308.MirrorC", {"center": v(38.1, -38.1) * mm, "radius": 2.55 * mm});
            skCircle(sketch, "E309.MirrorC", {"center": v(-190.5, -342.9) * mm, "radius": 2.55 * mm});
            skCircle(sketch, "E310.MirrorC", {"center": v(342.9, -419.1) * mm, "radius": 2.55 * mm});
            skCircle(sketch, "E311.MirrorC", {"center": v(304.8, -381) * mm, "radius": 2.55 * mm});
            skCircle(sketch, "E312.MirrorC", {"center": v(-190.5, -457.2) * mm, "radius": 2.55 * mm});
            skCircle(sketch, "E313.MirrorC", {"center": v(-304.8, -381) * mm, "radius": 2.55 * mm});
            skCircle(sketch, "E314.MirrorC", {"center": v(-190.5, -304.8) * mm, "radius": 2.55 * mm});
            skCircle(sketch, "E315.MirrorC", {"center": v(-114.3, -533.4) * mm, "radius": 2.55 * mm});
            skCircle(sketch, "E316.MirrorC", {"center": v(-114.3, -381) * mm, "radius": 2.55 * mm});
            skCircle(sketch, "E317.MirrorC", {"center": v(-152.4, -342.9) * mm, "radius": 2.55 * mm});
            skCircle(sketch, "E318.MirrorC", {"center": v(-152.4, -38.1) * mm, "radius": 2.55 * mm});
            skCircle(sketch, "E319.MirrorC", {"center": v(-228.6, -533.4) * mm, "radius": 2.55 * mm});
            skCircle(sketch, "E320.MirrorC", {"center": v(38.1, -190.5) * mm, "radius": 2.55 * mm});
            skCircle(sketch, "E321.MirrorC", {"center": v(-304.8, -114.3) * mm, "radius": 2.55 * mm});
            skCircle(sketch, "E322.MirrorC", {"center": v(76.2, -76.2) * mm, "radius": 2.55 * mm});
            skCircle(sketch, "E323.MirrorC", {"center": v(-152.4, -76.2) * mm, "radius": 2.55 * mm});
            skCircle(sketch, "E324.MirrorC", {"center": v(114.3, -266.7) * mm, "radius": 2.55 * mm});
            skCircle(sketch, "E325.MirrorC", {"center": v(-38.1, -381) * mm, "radius": 2.55 * mm});
            skCircle(sketch, "E326.MirrorC", {"center": v(-38.1, -342.9) * mm, "radius": 2.55 * mm});
            skCircle(sketch, "E327.MirrorC", {"center": v(76.2, -533.4) * mm, "radius": 2.55 * mm});
            skCircle(sketch, "E328.MirrorC", {"center": v(-228.6, -152.4) * mm, "radius": 2.55 * mm});
            skCircle(sketch, "E329.MirrorC", {"center": v(-38.1, -419.1) * mm, "radius": 2.55 * mm});
            skCircle(sketch, "E330.MirrorC", {"center": v(228.6, -228.6) * mm, "radius": 2.55 * mm});
            skCircle(sketch, "E331.MirrorC", {"center": v(-38.1, -228.6) * mm, "radius": 2.55 * mm});
            skCircle(sketch, "E332.MirrorC", {"center": v(-266.7, -266.7) * mm, "radius": 2.55 * mm});
            skCircle(sketch, "E333.MirrorC", {"center": v(304.8, -457.2) * mm, "radius": 2.55 * mm});
            skCircle(sketch, "E334.MirrorC", {"center": v(228.6, -419.1) * mm, "radius": 2.55 * mm});
            skCircle(sketch, "E335.MirrorC", {"center": v(342.9, -38.1) * mm, "radius": 2.55 * mm});
            skCircle(sketch, "E336.MirrorC", {"center": v(-152.4, -114.3) * mm, "radius": 2.55 * mm});
            skCircle(sketch, "E337.MirrorC", {"center": v(76.2, -152.4) * mm, "radius": 2.55 * mm});
            skCircle(sketch, "E338.MirrorC", {"center": v(342.9, -457.2) * mm, "radius": 2.55 * mm});
            skCircle(sketch, "E339.MirrorC", {"center": v(-266.7, -114.3) * mm, "radius": 2.55 * mm});
            skCircle(sketch, "E340.MirrorC", {"center": v(-342.9, -266.7) * mm, "radius": 2.55 * mm});
            skCircle(sketch, "E341.MirrorC", {"center": v(228.6, -495.3) * mm, "radius": 2.55 * mm});
            skCircle(sketch, "E342.MirrorC", {"center": v(-342.9, -38.1) * mm, "radius": 2.55 * mm});
            skCircle(sketch, "E343.MirrorC", {"center": v(-190.5, -381) * mm, "radius": 2.55 * mm});
            skCircle(sketch, "E344.MirrorC", {"center": v(-190.5, -114.3) * mm, "radius": 2.55 * mm});
            skCircle(sketch, "E345.MirrorC", {"center": v(114.3, -152.4) * mm, "radius": 2.55 * mm});
            skCircle(sketch, "E346.MirrorC", {"center": v(152.4, -533.4) * mm, "radius": 2.55 * mm});
            skCircle(sketch, "E347.MirrorC", {"center": v(-228.6, -457.2) * mm, "radius": 2.55 * mm});
            skCircle(sketch, "E348.MirrorC", {"center": v(-152.4, -457.2) * mm, "radius": 2.55 * mm});
            skCircle(sketch, "E349.MirrorC", {"center": v(-76.2, -266.7) * mm, "radius": 2.55 * mm});
            skCircle(sketch, "E350.MirrorC", {"center": v(-266.7, -419.1) * mm, "radius": 2.55 * mm});
            skCircle(sketch, "E351.MirrorC", {"center": v(190.5, -76.2) * mm, "radius": 2.55 * mm});
            skCircle(sketch, "E352.MirrorC", {"center": v(114.3, -342.9) * mm, "radius": 2.55 * mm});
            skCircle(sketch, "E353.MirrorC", {"center": v(76.2, -381) * mm, "radius": 2.55 * mm});
            skCircle(sketch, "E354.MirrorC", {"center": v(114.3, -228.6) * mm, "radius": 2.55 * mm});
            skCircle(sketch, "E355.MirrorC", {"center": v(76.2, -38.1) * mm, "radius": 2.55 * mm});
            skCircle(sketch, "E356.MirrorC", {"center": v(266.7, -457.2) * mm, "radius": 2.55 * mm});
            skCircle(sketch, "E357.MirrorC", {"center": v(38.1, -533.4) * mm, "radius": 2.55 * mm});
            skCircle(sketch, "E358.MirrorC", {"center": v(266.7, -381) * mm, "radius": 2.55 * mm});
            skCircle(sketch, "E359.MirrorC", {"center": v(228.6, -190.5) * mm, "radius": 2.55 * mm});
            skCircle(sketch, "E360.MirrorC", {"center": v(342.9, -342.9) * mm, "radius": 2.55 * mm});
            skCircle(sketch, "E361.MirrorC", {"center": v(-114.3, -38.1) * mm, "radius": 2.55 * mm});
            skCircle(sketch, "E362.MirrorC", {"center": v(-190.5, -152.4) * mm, "radius": 2.55 * mm});
            skCircle(sketch, "E363.MirrorC", {"center": v(342.9, -533.4) * mm, "radius": 2.55 * mm});
            skCircle(sketch, "E364.MirrorC", {"center": v(-190.5, -533.4) * mm, "radius": 2.55 * mm});
            skCircle(sketch, "E365.MirrorC", {"center": v(304.8, -495.3) * mm, "radius": 2.55 * mm});
            skCircle(sketch, "E366.MirrorC", {"center": v(266.7, -419.1) * mm, "radius": 2.55 * mm});
            skCircle(sketch, "E367.MirrorC", {"center": v(-266.7, -152.4) * mm, "radius": 2.55 * mm});
            skCircle(sketch, "E368.MirrorC", {"center": v(-228.6, -38.1) * mm, "radius": 2.55 * mm});
            skCircle(sketch, "E369.MirrorC", {"center": v(190.5, -457.2) * mm, "radius": 2.55 * mm});
            skCircle(sketch, "E370.MirrorC", {"center": v(190.5, -114.3) * mm, "radius": 2.55 * mm});
            skCircle(sketch, "E371.MirrorC", {"center": v(-304.8, -190.5) * mm, "radius": 2.55 * mm});
            skCircle(sketch, "E372.MirrorC", {"center": v(-114.3, -342.9) * mm, "radius": 2.55 * mm});
            skCircle(sketch, "E373.MirrorC", {"center": v(342.9, -266.7) * mm, "radius": 2.55 * mm});
            skCircle(sketch, "E374.MirrorC", {"center": v(228.6, -304.8) * mm, "radius": 2.55 * mm});
            skCircle(sketch, "E375.MirrorC", {"center": v(190.5, -419.1) * mm, "radius": 2.55 * mm});
            skCircle(sketch, "E376.MirrorC", {"center": v(-304.8, -304.8) * mm, "radius": 2.55 * mm});
            skCircle(sketch, "E377.MirrorC", {"center": v(-38.1, -76.2) * mm, "radius": 2.55 * mm});
            skCircle(sketch, "E378.MirrorC", {"center": v(-152.4, -381) * mm, "radius": 2.55 * mm});
            skCircle(sketch, "E379.MirrorC", {"center": v(-266.7, -457.2) * mm, "radius": 2.55 * mm});
            skCircle(sketch, "E380.MirrorC", {"center": v(-304.8, -266.7) * mm, "radius": 2.55 * mm});
            skCircle(sketch, "E381.MirrorC", {"center": v(-114.3, -76.2) * mm, "radius": 2.55 * mm});
            skCircle(sketch, "E382.MirrorC", {"center": v(76.2, -342.9) * mm, "radius": 2.55 * mm});
            skCircle(sketch, "E383.MirrorC", {"center": v(266.7, -76.2) * mm, "radius": 2.55 * mm});
            skCircle(sketch, "E384.MirrorC", {"center": v(152.4, -114.3) * mm, "radius": 2.55 * mm});
            skCircle(sketch, "E385.MirrorC", {"center": v(38.1, -152.4) * mm, "radius": 2.55 * mm});
            skCircle(sketch, "E386.MirrorC", {"center": v(152.4, -152.4) * mm, "radius": 2.55 * mm});
            skCircle(sketch, "E387.MirrorC", {"center": v(190.5, -342.9) * mm, "radius": 2.55 * mm});
            skCircle(sketch, "E388.MirrorC", {"center": v(-304.8, -228.6) * mm, "radius": 2.55 * mm});
            skCircle(sketch, "E389.MirrorC", {"center": v(304.8, -152.4) * mm, "radius": 2.55 * mm});
            skCircle(sketch, "E390.MirrorC", {"center": v(114.3, -38.1) * mm, "radius": 2.55 * mm});
            skCircle(sketch, "E391.MirrorC", {"center": v(114.3, -533.4) * mm, "radius": 2.55 * mm});
            skCircle(sketch, "E392.MirrorC", {"center": v(152.4, -457.2) * mm, "radius": 2.55 * mm});
            skCircle(sketch, "E393.MirrorC", {"center": v(114.3, -381) * mm, "radius": 2.55 * mm});
            skCircle(sketch, "E394.MirrorC", {"center": v(190.5, -152.4) * mm, "radius": 2.55 * mm});
            skCircle(sketch, "E395.MirrorC", {"center": v(228.6, -342.9) * mm, "radius": 2.55 * mm});
            skCircle(sketch, "E396.MirrorC", {"center": v(152.4, -342.9) * mm, "radius": 2.55 * mm});
            skCircle(sketch, "E397.MirrorC", {"center": v(-76.2, -457.2) * mm, "radius": 2.55 * mm});
            skCircle(sketch, "E398.MirrorC", {"center": v(190.5, -38.1) * mm, "radius": 2.55 * mm});
            skCircle(sketch, "E399.MirrorC", {"center": v(-304.8, -457.2) * mm, "radius": 2.55 * mm});
            skCircle(sketch, "E400.MirrorC", {"center": v(152.4, -419.1) * mm, "radius": 2.55 * mm});
            skCircle(sketch, "E401.MirrorC", {"center": v(-342.9, -419.1) * mm, "radius": 2.55 * mm});
            skCircle(sketch, "E402.MirrorC", {"center": v(-76.2, -190.5) * mm, "radius": 2.55 * mm});
            skCircle(sketch, "E403.MirrorC", {"center": v(-152.4, -152.4) * mm, "radius": 2.55 * mm});
            skCircle(sketch, "E404.MirrorC", {"center": v(114.3, -304.8) * mm, "radius": 2.55 * mm});
            skCircle(sketch, "E405.MirrorC", {"center": v(76.2, -495.3) * mm, "radius": 2.55 * mm});
            skCircle(sketch, "E406.MirrorC", {"center": v(228.6, -152.4) * mm, "radius": 2.55 * mm});
            skCircle(sketch, "E407.MirrorC", {"center": v(304.8, -304.8) * mm, "radius": 2.55 * mm});
            skCircle(sketch, "E408.MirrorC", {"center": v(-190.5, -495.3) * mm, "radius": 2.55 * mm});
            skCircle(sketch, "E409.MirrorC", {"center": v(190.5, -190.5) * mm, "radius": 2.55 * mm});
            skCircle(sketch, "E410.MirrorC", {"center": v(228.6, -381) * mm, "radius": 2.55 * mm});
            skSolve(sketch);
        }
        {
            var Q0;
            Q0=makeQuery(id+"F0.imprint","IMPRINT",FACE,{"disambiguationData":[TD([[makeQuery(id+"F0.imprint","IMPRINT",EDGE,{"derivedFrom":sQuery(id+"F0.wireOp",EDGE,"E0.bottom")}),1.0]])]});
            extrude(context, id + "F1", {"entities" : qUnion([Q0]), "depth" : 19.05 * mm, "offsetDistance" : 25.4 * mm});
        }
        {
            var Q0;
            Q0=makeQuery(id+"F1.opExtrude","CAP_FACE",FACE,{"disambiguationData":[OSD([sQuery(id+"F0.wireOp",EDGE,"E0.bottom"),sQuery(id+"F0.wireOp",EDGE,"E0.top"),sQuery(id+"F0.wireOp",EDGE,"E0.left"),sQuery(id+"F0.wireOp",EDGE,"E0.right"),sQuery(id+"F0.wireOp",EDGE,"E3.1.0.0"),sQuery(id+"F0.wireOp",EDGE,"E3.1.1.0"),sQuery(id+"F0.wireOp",EDGE,"E3.1.2.0"),sQuery(id+"F0.wireOp",EDGE,"E3.1.3.0"),sQuery(id+"F0.wireOp",EDGE,"E3.1.4.0"),sQuery(id+"F0.wireOp",EDGE,"E3.1.5.0"),sQuery(id+"F0.wireOp",EDGE,"E3.1.6.0"),sQuery(id+"F0.wireOp",EDGE,"E3.1.7.0"),sQuery(id+"F0.wireOp",EDGE,"E3.1.8.0"),sQuery(id+"F0.wireOp",EDGE,"E3.1.9.0"),sQuery(id+"F0.wireOp",EDGE,"E3.1.10.0"),sQuery(id+"F0.wireOp",EDGE,"E3.2.0.0"),sQuery(id+"F0.wireOp",EDGE,"E3.2.1.0"),sQuery(id+"F0.wireOp",EDGE,"E3.2.2.0"),sQuery(id+"F0.wireOp",EDGE,"E3.2.3.0"),sQuery(id+"F0.wireOp",EDGE,"E3.2.4.0"),sQuery(id+"F0.wireOp",EDGE,"E3.2.5.0"),sQuery(id+"F0.wireOp",EDGE,"E3.2.6.0"),sQuery(id+"F0.wireOp",EDGE,"E3.2.7.0"),sQuery(id+"F0.wireOp",EDGE,"E3.2.8.0"),sQuery(id+"F0.wireOp",EDGE,"E3.2.9.0"),sQuery(id+"F0.wireOp",EDGE,"E3.2.10.0"),sQuery(id+"F0.wireOp",EDGE,"E3.3.0.0"),sQuery(id+"F0.wireOp",EDGE,"E3.3.1.0"),sQuery(id+"F0.wireOp",EDGE,"E3.3.2.0"),sQuery(id+"F0.wireOp",EDGE,"E3.3.3.0"),sQuery(id+"F0.wireOp",EDGE,"E3.3.4.0"),sQuery(id+"F0.wireOp",EDGE,"E3.3.5.0"),sQuery(id+"F0.wireOp",EDGE,"E3.3.6.0"),sQuery(id+"F0.wireOp",EDGE,"E3.3.7.0"),sQuery(id+"F0.wireOp",EDGE,"E3.3.8.0"),sQuery(id+"F0.wireOp",EDGE,"E3.3.9.0"),sQuery(id+"F0.wireOp",EDGE,"E3.3.10.0"),sQuery(id+"F0.wireOp",EDGE,"E3.4.0.0"),sQuery(id+"F0.wireOp",EDGE,"E3.4.1.0"),sQuery(id+"F0.wireOp",EDGE,"E3.4.2.0"),sQuery(id+"F0.wireOp",EDGE,"E3.4.3.0"),sQuery(id+"F0.wireOp",EDGE,"E3.4.4.0"),sQuery(id+"F0.wireOp",EDGE,"E3.4.5.0"),sQuery(id+"F0.wireOp",EDGE,"E3.4.6.0"),sQuery(id+"F0.wireOp",EDGE,"E3.4.7.0"),sQuery(id+"F0.wireOp",EDGE,"E3.4.8.0"),sQuery(id+"F0.wireOp",EDGE,"E3.4.9.0"),sQuery(id+"F0.wireOp",EDGE,"E3.4.10.0"),sQuery(id+"F0.wireOp",EDGE,"E3.5.0.0"),sQuery(id+"F0.wireOp",EDGE,"E3.5.1.0"),sQuery(id+"F0.wireOp",EDGE,"E3.5.2.0"),sQuery(id+"F0.wireOp",EDGE,"E3.5.3.0"),sQuery(id+"F0.wireOp",EDGE,"E3.5.4.0"),sQuery(id+"F0.wireOp",EDGE,"E3.5.5.0"),sQuery(id+"F0.wireOp",EDGE,"E3.5.6.0"),sQuery(id+"F0.wireOp",EDGE,"E3.5.7.0"),sQuery(id+"F0.wireOp",EDGE,"E3.5.8.0"),sQuery(id+"F0.wireOp",EDGE,"E3.5.9.0"),sQuery(id+"F0.wireOp",EDGE,"E3.5.10.0"),sQuery(id+"F0.wireOp",EDGE,"E3.6.0.0"),sQuery(id+"F0.wireOp",EDGE,"E3.6.1.0"),sQuery(id+"F0.wireOp",EDGE,"E3.6.2.0"),sQuery(id+"F0.wireOp",EDGE,"E3.6.3.0"),sQuery(id+"F0.wireOp",EDGE,"E3.6.4.0"),sQuery(id+"F0.wireOp",EDGE,"E3.6.5.0"),sQuery(id+"F0.wireOp",EDGE,"E3.6.6.0"),sQuery(id+"F0.wireOp",EDGE,"E3.6.7.0"),sQuery(id+"F0.wireOp",EDGE,"E3.6.8.0"),sQuery(id+"F0.wireOp",EDGE,"E3.6.9.0"),sQuery(id+"F0.wireOp",EDGE,"E3.6.10.0"),sQuery(id+"F0.wireOp",EDGE,"E3.7.0.0"),sQuery(id+"F0.wireOp",EDGE,"E3.7.1.0"),sQuery(id+"F0.wireOp",EDGE,"E3.7.2.0"),sQuery(id+"F0.wireOp",EDGE,"E3.7.3.0"),sQuery(id+"F0.wireOp",EDGE,"E3.7.4.0"),sQuery(id+"F0.wireOp",EDGE,"E3.7.5.0"),sQuery(id+"F0.wireOp",EDGE,"E3.7.6.0"),sQuery(id+"F0.wireOp",EDGE,"E3.7.7.0"),sQuery(id+"F0.wireOp",EDGE,"E3.7.8.0"),sQuery(id+"F0.wireOp",EDGE,"E3.7.9.0"),sQuery(id+"F0.wireOp",EDGE,"E3.7.10.0"),sQuery(id+"F0.wireOp",EDGE,"E4.0.1.11"),sQuery(id+"F0.wireOp",EDGE,"E4.0.2.11"),sQuery(id+"F0.wireOp",EDGE,"E4.0.3.11"),sQuery(id+"F0.wireOp",EDGE,"E4.0.4.11"),sQuery(id+"F0.wireOp",EDGE,"E4.0.5.11"),sQuery(id+"F0.wireOp",EDGE,"E4.0.6.11"),sQuery(id+"F0.wireOp",EDGE,"E4.0.7.11"),sQuery(id+"F0.wireOp",EDGE,"E5.0.1.12"),sQuery(id+"F0.wireOp",EDGE,"E5.0.1.13"),sQuery(id+"F0.wireOp",EDGE,"E5.0.1.14"),sQuery(id+"F0.wireOp",EDGE,"E5.0.2.12"),sQuery(id+"F0.wireOp",EDGE,"E5.0.2.13"),sQuery(id+"F0.wireOp",EDGE,"E5.0.2.14"),sQuery(id+"F0.wireOp",EDGE,"E5.0.3.12"),sQuery(id+"F0.wireOp",EDGE,"E5.0.3.13"),sQuery(id+"F0.wireOp",EDGE,"E5.0.3.14"),sQuery(id+"F0.wireOp",EDGE,"E5.0.4.12"),sQuery(id+"F0.wireOp",EDGE,"E5.0.4.13"),sQuery(id+"F0.wireOp",EDGE,"E5.0.4.14"),sQuery(id+"F0.wireOp",EDGE,"E5.0.5.12"),sQuery(id+"F0.wireOp",EDGE,"E5.0.5.13"),sQuery(id+"F0.wireOp",EDGE,"E5.0.5.14"),sQuery(id+"F0.wireOp",EDGE,"E5.0.6.12"),sQuery(id+"F0.wireOp",EDGE,"E5.0.6.13"),sQuery(id+"F0.wireOp",EDGE,"E5.0.6.14"),sQuery(id+"F0.wireOp",EDGE,"E5.0.7.12"),sQuery(id+"F0.wireOp",EDGE,"E5.0.7.13"),sQuery(id+"F0.wireOp",EDGE,"E5.0.7.14"),sQuery(id+"F0.wireOp",EDGE,"E6.0.8.0"),sQuery(id+"F0.wireOp",EDGE,"E6.0.8.1"),sQuery(id+"F0.wireOp",EDGE,"E6.0.8.2"),sQuery(id+"F0.wireOp",EDGE,"E6.0.8.3"),sQuery(id+"F0.wireOp",EDGE,"E6.0.8.4"),sQuery(id+"F0.wireOp",EDGE,"E6.0.8.5"),sQuery(id+"F0.wireOp",EDGE,"E6.0.8.6"),sQuery(id+"F0.wireOp",EDGE,"E6.0.8.7"),sQuery(id+"F0.wireOp",EDGE,"E6.0.8.8"),sQuery(id+"F0.wireOp",EDGE,"E6.0.8.9"),sQuery(id+"F0.wireOp",EDGE,"E6.0.8.10"),sQuery(id+"F0.wireOp",EDGE,"E6.0.8.11"),sQuery(id+"F0.wireOp",EDGE,"E6.0.8.12"),sQuery(id+"F0.wireOp",EDGE,"E6.0.8.13"),sQuery(id+"F0.wireOp",EDGE,"E6.0.8.14"),sQuery(id+"F0.wireOp",EDGE,"E6.0.9.0"),sQuery(id+"F0.wireOp",EDGE,"E6.0.9.1"),sQuery(id+"F0.wireOp",EDGE,"E6.0.9.2"),sQuery(id+"F0.wireOp",EDGE,"E6.0.9.3"),sQuery(id+"F0.wireOp",EDGE,"E6.0.9.4"),sQuery(id+"F0.wireOp",EDGE,"E6.0.9.5"),sQuery(id+"F0.wireOp",EDGE,"E6.0.9.6"),sQuery(id+"F0.wireOp",EDGE,"E6.0.9.7"),sQuery(id+"F0.wireOp",EDGE,"E6.0.9.8"),sQuery(id+"F0.wireOp",EDGE,"E6.0.9.9"),sQuery(id+"F0.wireOp",EDGE,"E6.0.9.10"),sQuery(id+"F0.wireOp",EDGE,"E6.0.9.11"),sQuery(id+"F0.wireOp",EDGE,"E6.0.9.12"),sQuery(id+"F0.wireOp",EDGE,"E6.0.9.13"),sQuery(id+"F0.wireOp",EDGE,"E6.0.9.14"),sQuery(id+"F0.wireOp",EDGE,"E3.0.1.0"),sQuery(id+"F0.wireOp",EDGE,"E8.MirrorC"),sQuery(id+"F0.wireOp",EDGE,"E9.MirrorC"),sQuery(id+"F0.wireOp",EDGE,"E10.MirrorC"),sQuery(id+"F0.wireOp",EDGE,"E11.MirrorC"),sQuery(id+"F0.wireOp",EDGE,"E12.MirrorC"),sQuery(id+"F0.wireOp",EDGE,"E13.MirrorC"),sQuery(id+"F0.wireOp",EDGE,"E14.MirrorC"),sQuery(id+"F0.wireOp",EDGE,"E15.MirrorC"),sQuery(id+"F0.wireOp",EDGE,"E16.MirrorC"),sQuery(id+"F0.wireOp",EDGE,"E17.MirrorC"),sQuery(id+"F0.wireOp",EDGE,"E18.MirrorC"),sQuery(id+"F0.wireOp",EDGE,"E19.MirrorC"),sQuery(id+"F0.wireOp",EDGE,"E20.MirrorC"),sQuery(id+"F0.wireOp",EDGE,"E21.MirrorC"),sQuery(id+"F0.wireOp",EDGE,"E22.MirrorC"),sQuery(id+"F0.wireOp",EDGE,"E23.MirrorC"),sQuery(id+"F0.wireOp",EDGE,"E24.MirrorC"),sQuery(id+"F0.wireOp",EDGE,"E25.MirrorC"),sQuery(id+"F0.wireOp",EDGE,"E26.MirrorC"),sQuery(id+"F0.wireOp",EDGE,"E27.MirrorC"),sQuery(id+"F0.wireOp",EDGE,"E28.MirrorC"),sQuery(id+"F0.wireOp",EDGE,"E29.MirrorC"),sQuery(id+"F0.wireOp",EDGE,"E30.MirrorC"),sQuery(id+"F0.wireOp",EDGE,"E31.MirrorC"),sQuery(id+"F0.wireOp",EDGE,"E32.MirrorC"),sQuery(id+"F0.wireOp",EDGE,"E33.MirrorC"),sQuery(id+"F0.wireOp",EDGE,"E4.0.0.11"),sQuery(id+"F0.wireOp",EDGE,"E34.MirrorC"),sQuery(id+"F0.wireOp",EDGE,"E35.MirrorC"),sQuery(id+"F0.wireOp",EDGE,"E3.0.4.0"),sQuery(id+"F0.wireOp",EDGE,"E3.0.6.0"),sQuery(id+"F0.wireOp",EDGE,"E3.0.7.0"),sQuery(id+"F0.wireOp",EDGE,"E36.MirrorC"),sQuery(id+"F0.wireOp",EDGE,"E37.MirrorC"),sQuery(id+"F0.wireOp",EDGE,"E38.MirrorC"),sQuery(id+"F0.wireOp",EDGE,"E39.MirrorC"),sQuery(id+"F0.wireOp",EDGE,"E40.MirrorC"),sQuery(id+"F0.wireOp",EDGE,"E41.MirrorC"),sQuery(id+"F0.wireOp",EDGE,"E42.MirrorC"),sQuery(id+"F0.wireOp",EDGE,"E3.0.3.0"),sQuery(id+"F0.wireOp",EDGE,"E43.MirrorC"),sQuery(id+"F0.wireOp",EDGE,"E44.MirrorC"),sQuery(id+"F0.wireOp",EDGE,"E45.MirrorC"),sQuery(id+"F0.wireOp",EDGE,"E46.MirrorC"),sQuery(id+"F0.wireOp",EDGE,"E47.MirrorC"),sQuery(id+"F0.wireOp",EDGE,"E48.MirrorC"),sQuery(id+"F0.wireOp",EDGE,"E49.MirrorC"),sQuery(id+"F0.wireOp",EDGE,"E50.MirrorC"),sQuery(id+"F0.wireOp",EDGE,"E51.MirrorC"),sQuery(id+"F0.wireOp",EDGE,"E52.MirrorC"),sQuery(id+"F0.wireOp",EDGE,"E53.MirrorC"),sQuery(id+"F0.wireOp",EDGE,"E54.MirrorC"),sQuery(id+"F0.wireOp",EDGE,"E55.MirrorC"),sQuery(id+"F0.wireOp",EDGE,"E56.MirrorC"),sQuery(id+"F0.wireOp",EDGE,"E5.0.0.13"),sQuery(id+"F0.wireOp",EDGE,"E57.MirrorC"),sQuery(id+"F0.wireOp",EDGE,"E58.MirrorC"),sQuery(id+"F0.wireOp",EDGE,"E59.MirrorC"),sQuery(id+"F0.wireOp",EDGE,"E60.MirrorC"),sQuery(id+"F0.wireOp",EDGE,"E61.MirrorC"),sQuery(id+"F0.wireOp",EDGE,"E62.MirrorC"),sQuery(id+"F0.wireOp",EDGE,"E63.MirrorC"),sQuery(id+"F0.wireOp",EDGE,"E64.MirrorC"),sQuery(id+"F0.wireOp",EDGE,"E65.MirrorC"),sQuery(id+"F0.wireOp",EDGE,"E66.MirrorC"),sQuery(id+"F0.wireOp",EDGE,"E67.MirrorC"),sQuery(id+"F0.wireOp",EDGE,"E68.MirrorC"),sQuery(id+"F0.wireOp",EDGE,"E69.MirrorC"),sQuery(id+"F0.wireOp",EDGE,"E70.MirrorC"),sQuery(id+"F0.wireOp",EDGE,"E5.0.0.12"),sQuery(id+"F0.wireOp",EDGE,"E71.MirrorC"),sQuery(id+"F0.wireOp",EDGE,"E72.MirrorC"),sQuery(id+"F0.wireOp",EDGE,"E73.MirrorC"),sQuery(id+"F0.wireOp",EDGE,"E74.MirrorC"),sQuery(id+"F0.wireOp",EDGE,"E75.MirrorC"),sQuery(id+"F0.wireOp",EDGE,"E76.MirrorC"),sQuery(id+"F0.wireOp",EDGE,"E3.0.5.0"),sQuery(id+"F0.wireOp",EDGE,"E77.MirrorC"),sQuery(id+"F0.wireOp",EDGE,"E78.MirrorC"),sQuery(id+"F0.wireOp",EDGE,"E79.MirrorC"),sQuery(id+"F0.wireOp",EDGE,"E80.MirrorC"),sQuery(id+"F0.wireOp",EDGE,"E81.MirrorC"),sQuery(id+"F0.wireOp",EDGE,"E82.MirrorC"),sQuery(id+"F0.wireOp",EDGE,"E83.MirrorC"),sQuery(id+"F0.wireOp",EDGE,"E84.MirrorC"),sQuery(id+"F0.wireOp",EDGE,"E85.MirrorC"),sQuery(id+"F0.wireOp",EDGE,"E86.MirrorC"),sQuery(id+"F0.wireOp",EDGE,"E87.MirrorC"),sQuery(id+"F0.wireOp",EDGE,"E88.MirrorC"),sQuery(id+"F0.wireOp",EDGE,"E89.MirrorC"),sQuery(id+"F0.wireOp",EDGE,"E90.MirrorC"),sQuery(id+"F0.wireOp",EDGE,"E91.MirrorC"),sQuery(id+"F0.wireOp",EDGE,"E92.MirrorC"),sQuery(id+"F0.wireOp",EDGE,"E93.MirrorC"),sQuery(id+"F0.wireOp",EDGE,"E94.MirrorC"),sQuery(id+"F0.wireOp",EDGE,"E95.MirrorC"),sQuery(id+"F0.wireOp",EDGE,"E96.MirrorC"),sQuery(id+"F0.wireOp",EDGE,"E97.MirrorC"),sQuery(id+"F0.wireOp",EDGE,"E98.MirrorC"),sQuery(id+"F0.wireOp",EDGE,"E3.0.2.0"),sQuery(id+"F0.wireOp",EDGE,"E99.MirrorC"),sQuery(id+"F0.wireOp",EDGE,"E100.MirrorC"),sQuery(id+"F0.wireOp",EDGE,"E101.MirrorC"),sQuery(id+"F0.wireOp",EDGE,"E5.0.0.14"),sQuery(id+"F0.wireOp",EDGE,"E102.MirrorC"),sQuery(id+"F0.wireOp",EDGE,"E103.MirrorC"),sQuery(id+"F0.wireOp",EDGE,"E104.MirrorC"),sQuery(id+"F0.wireOp",EDGE,"E105.MirrorC"),sQuery(id+"F0.wireOp",EDGE,"E106.MirrorC"),sQuery(id+"F0.wireOp",EDGE,"E107.MirrorC"),sQuery(id+"F0.wireOp",EDGE,"E108.MirrorC"),sQuery(id+"F0.wireOp",EDGE,"E109.MirrorC"),sQuery(id+"F0.wireOp",EDGE,"E110.MirrorC"),sQuery(id+"F0.wireOp",EDGE,"E111.MirrorC"),sQuery(id+"F0.wireOp",EDGE,"E112.MirrorC"),sQuery(id+"F0.wireOp",EDGE,"E113.MirrorC"),sQuery(id+"F0.wireOp",EDGE,"E114.MirrorC"),sQuery(id+"F0.wireOp",EDGE,"E115.MirrorC"),sQuery(id+"F0.wireOp",EDGE,"E116.MirrorC"),sQuery(id+"F0.wireOp",EDGE,"E117.MirrorC"),sQuery(id+"F0.wireOp",EDGE,"E118.MirrorC"),sQuery(id+"F0.wireOp",EDGE,"E119.MirrorC"),sQuery(id+"F0.wireOp",EDGE,"E120.MirrorC"),sQuery(id+"F0.wireOp",EDGE,"E121.MirrorC"),sQuery(id+"F0.wireOp",EDGE,"E122.MirrorC"),sQuery(id+"F0.wireOp",EDGE,"E123.MirrorC"),sQuery(id+"F0.wireOp",EDGE,"E124.MirrorC"),sQuery(id+"F0.wireOp",EDGE,"E125.MirrorC"),sQuery(id+"F0.wireOp",EDGE,"E126.MirrorC"),sQuery(id+"F0.wireOp",EDGE,"E127.MirrorC"),sQuery(id+"F0.wireOp",EDGE,"E3.0.8.0"),sQuery(id+"F0.wireOp",EDGE,"E3.0.10.0"),sQuery(id+"F0.wireOp",EDGE,"E128.MirrorC"),sQuery(id+"F0.wireOp",EDGE,"E129.MirrorC"),sQuery(id+"F0.wireOp",EDGE,"E3.0.9.0"),sQuery(id+"F0.wireOp",EDGE,"E130.MirrorC"),sQuery(id+"F0.wireOp",EDGE,"E131.MirrorC"),sQuery(id+"F0.wireOp",EDGE,"E132.MirrorC"),sQuery(id+"F0.wireOp",EDGE,"E133.MirrorC"),sQuery(id+"F0.wireOp",EDGE,"E2"),sQuery(id+"F0.wireOp",EDGE,"E135.MirrorC"),sQuery(id+"F0.wireOp",EDGE,"E136.MirrorC"),sQuery(id+"F0.wireOp",EDGE,"E137.MirrorC"),sQuery(id+"F0.wireOp",EDGE,"E138.MirrorC"),sQuery(id+"F0.wireOp",EDGE,"E139.MirrorC"),sQuery(id+"F0.wireOp",EDGE,"E140.MirrorC"),sQuery(id+"F0.wireOp",EDGE,"E141.MirrorC"),sQuery(id+"F0.wireOp",EDGE,"E142.MirrorC"),sQuery(id+"F0.wireOp",EDGE,"E143.MirrorC"),sQuery(id+"F0.wireOp",EDGE,"E145.MirrorC"),sQuery(id+"F0.wireOp",EDGE,"E147.MirrorC"),sQuery(id+"F0.wireOp",EDGE,"E148.MirrorC"),sQuery(id+"F0.wireOp",EDGE,"E158.MirrorC"),sQuery(id+"F0.wireOp",EDGE,"E151.MirrorC"),sQuery(id+"F0.wireOp",EDGE,"E154.MirrorC"),sQuery(id+"F0.wireOp",EDGE,"E155.MirrorC"),sQuery(id+"F0.wireOp",EDGE,"E146.MirrorC"),sQuery(id+"F0.wireOp",EDGE,"E156.MirrorC"),sQuery(id+"F0.wireOp",EDGE,"E152.MirrorC"),sQuery(id+"F0.wireOp",EDGE,"E149.MirrorC"),sQuery(id+"F0.wireOp",EDGE,"E153.MirrorC"),sQuery(id+"F0.wireOp",EDGE,"E150.MirrorC"),sQuery(id+"F0.wireOp",EDGE,"E157.MirrorC"),sQuery(id+"F0.wireOp",EDGE,"E159.MirrorC"),sQuery(id+"F0.wireOp",EDGE,"E160.MirrorC"),sQuery(id+"F0.wireOp",EDGE,"E161.MirrorC"),sQuery(id+"F0.wireOp",EDGE,"E162.MirrorC"),sQuery(id+"F0.wireOp",EDGE,"E163.MirrorC"),sQuery(id+"F0.wireOp",EDGE,"E164.MirrorC"),sQuery(id+"F0.wireOp",EDGE,"E165.MirrorC"),sQuery(id+"F0.wireOp",EDGE,"E166.MirrorC"),sQuery(id+"F0.wireOp",EDGE,"E167.MirrorC"),sQuery(id+"F0.wireOp",EDGE,"E168.MirrorC"),sQuery(id+"F0.wireOp",EDGE,"E169.MirrorC"),sQuery(id+"F0.wireOp",EDGE,"E170.MirrorC"),sQuery(id+"F0.wireOp",EDGE,"E171.MirrorC"),sQuery(id+"F0.wireOp",EDGE,"E172.MirrorC"),sQuery(id+"F0.wireOp",EDGE,"E173.MirrorC"),sQuery(id+"F0.wireOp",EDGE,"E174.MirrorC"),sQuery(id+"F0.wireOp",EDGE,"E175.MirrorC"),sQuery(id+"F0.wireOp",EDGE,"E176.MirrorC"),sQuery(id+"F0.wireOp",EDGE,"E177.MirrorC"),sQuery(id+"F0.wireOp",EDGE,"E178.MirrorC"),sQuery(id+"F0.wireOp",EDGE,"E179.MirrorC"),sQuery(id+"F0.wireOp",EDGE,"E180.MirrorC"),sQuery(id+"F0.wireOp",EDGE,"E181.MirrorC"),sQuery(id+"F0.wireOp",EDGE,"E182.MirrorC"),sQuery(id+"F0.wireOp",EDGE,"E183.MirrorC"),sQuery(id+"F0.wireOp",EDGE,"E184.MirrorC"),sQuery(id+"F0.wireOp",EDGE,"E185.MirrorC"),sQuery(id+"F0.wireOp",EDGE,"E186.MirrorC"),sQuery(id+"F0.wireOp",EDGE,"E187.MirrorC"),sQuery(id+"F0.wireOp",EDGE,"E188.MirrorC"),sQuery(id+"F0.wireOp",EDGE,"E189.MirrorC"),sQuery(id+"F0.wireOp",EDGE,"E190.MirrorC"),sQuery(id+"F0.wireOp",EDGE,"E191.MirrorC"),sQuery(id+"F0.wireOp",EDGE,"E192.MirrorC"),sQuery(id+"F0.wireOp",EDGE,"E193.MirrorC"),sQuery(id+"F0.wireOp",EDGE,"E194.MirrorC"),sQuery(id+"F0.wireOp",EDGE,"E195.MirrorC"),sQuery(id+"F0.wireOp",EDGE,"E196.MirrorC"),sQuery(id+"F0.wireOp",EDGE,"E197.MirrorC"),sQuery(id+"F0.wireOp",EDGE,"E198.MirrorC"),sQuery(id+"F0.wireOp",EDGE,"E199.MirrorC"),sQuery(id+"F0.wireOp",EDGE,"E200.MirrorC"),sQuery(id+"F0.wireOp",EDGE,"E201.MirrorC"),sQuery(id+"F0.wireOp",EDGE,"E202.MirrorC"),sQuery(id+"F0.wireOp",EDGE,"E203.MirrorC"),sQuery(id+"F0.wireOp",EDGE,"E204.MirrorC"),sQuery(id+"F0.wireOp",EDGE,"E205.MirrorC"),sQuery(id+"F0.wireOp",EDGE,"E206.MirrorC"),sQuery(id+"F0.wireOp",EDGE,"E207.MirrorC"),sQuery(id+"F0.wireOp",EDGE,"E208.MirrorC"),sQuery(id+"F0.wireOp",EDGE,"E209.MirrorC"),sQuery(id+"F0.wireOp",EDGE,"E210.MirrorC"),sQuery(id+"F0.wireOp",EDGE,"E211.MirrorC"),sQuery(id+"F0.wireOp",EDGE,"E212.MirrorC"),sQuery(id+"F0.wireOp",EDGE,"E213.MirrorC"),sQuery(id+"F0.wireOp",EDGE,"E214.MirrorC"),sQuery(id+"F0.wireOp",EDGE,"E215.MirrorC"),sQuery(id+"F0.wireOp",EDGE,"E216.MirrorC"),sQuery(id+"F0.wireOp",EDGE,"E217.MirrorC"),sQuery(id+"F0.wireOp",EDGE,"E218.MirrorC"),sQuery(id+"F0.wireOp",EDGE,"E219.MirrorC"),sQuery(id+"F0.wireOp",EDGE,"E220.MirrorC"),sQuery(id+"F0.wireOp",EDGE,"E221.MirrorC"),sQuery(id+"F0.wireOp",EDGE,"E222.MirrorC"),sQuery(id+"F0.wireOp",EDGE,"E223.MirrorC"),sQuery(id+"F0.wireOp",EDGE,"E224.MirrorC"),sQuery(id+"F0.wireOp",EDGE,"E225.MirrorC"),sQuery(id+"F0.wireOp",EDGE,"E226.MirrorC"),sQuery(id+"F0.wireOp",EDGE,"E227.MirrorC"),sQuery(id+"F0.wireOp",EDGE,"E228.MirrorC"),sQuery(id+"F0.wireOp",EDGE,"E229.MirrorC"),sQuery(id+"F0.wireOp",EDGE,"E230.MirrorC"),sQuery(id+"F0.wireOp",EDGE,"E231.MirrorC"),sQuery(id+"F0.wireOp",EDGE,"E232.MirrorC"),sQuery(id+"F0.wireOp",EDGE,"E233.MirrorC"),sQuery(id+"F0.wireOp",EDGE,"E234.MirrorC"),sQuery(id+"F0.wireOp",EDGE,"E235.MirrorC"),sQuery(id+"F0.wireOp",EDGE,"E236.MirrorC"),sQuery(id+"F0.wireOp",EDGE,"E237.MirrorC"),sQuery(id+"F0.wireOp",EDGE,"E238.MirrorC"),sQuery(id+"F0.wireOp",EDGE,"E239.MirrorC"),sQuery(id+"F0.wireOp",EDGE,"E240.MirrorC"),sQuery(id+"F0.wireOp",EDGE,"E241.MirrorC"),sQuery(id+"F0.wireOp",EDGE,"E242.MirrorC"),sQuery(id+"F0.wireOp",EDGE,"E243.MirrorC"),sQuery(id+"F0.wireOp",EDGE,"E244.MirrorC"),sQuery(id+"F0.wireOp",EDGE,"E245.MirrorC"),sQuery(id+"F0.wireOp",EDGE,"E246.MirrorC"),sQuery(id+"F0.wireOp",EDGE,"E247.MirrorC"),sQuery(id+"F0.wireOp",EDGE,"E248.MirrorC"),sQuery(id+"F0.wireOp",EDGE,"E249.MirrorC"),sQuery(id+"F0.wireOp",EDGE,"E250.MirrorC"),sQuery(id+"F0.wireOp",EDGE,"E251.MirrorC"),sQuery(id+"F0.wireOp",EDGE,"E252.MirrorC"),sQuery(id+"F0.wireOp",EDGE,"E253.MirrorC"),sQuery(id+"F0.wireOp",EDGE,"E254.MirrorC"),sQuery(id+"F0.wireOp",EDGE,"E255.MirrorC"),sQuery(id+"F0.wireOp",EDGE,"E256.MirrorC"),sQuery(id+"F0.wireOp",EDGE,"E257.MirrorC"),sQuery(id+"F0.wireOp",EDGE,"E258.MirrorC"),sQuery(id+"F0.wireOp",EDGE,"E259.MirrorC"),sQuery(id+"F0.wireOp",EDGE,"E260.MirrorC"),sQuery(id+"F0.wireOp",EDGE,"E261.MirrorC"),sQuery(id+"F0.wireOp",EDGE,"E262.MirrorC"),sQuery(id+"F0.wireOp",EDGE,"E263.MirrorC"),sQuery(id+"F0.wireOp",EDGE,"E264.MirrorC"),sQuery(id+"F0.wireOp",EDGE,"E265.MirrorC"),sQuery(id+"F0.wireOp",EDGE,"E266.MirrorC"),sQuery(id+"F0.wireOp",EDGE,"E267.MirrorC"),sQuery(id+"F0.wireOp",EDGE,"E268.MirrorC"),sQuery(id+"F0.wireOp",EDGE,"E269.MirrorC"),sQuery(id+"F0.wireOp",EDGE,"E270.MirrorC"),sQuery(id+"F0.wireOp",EDGE,"E271.MirrorC"),sQuery(id+"F0.wireOp",EDGE,"E272.MirrorC"),sQuery(id+"F0.wireOp",EDGE,"E273.MirrorC"),sQuery(id+"F0.wireOp",EDGE,"E274.MirrorC"),sQuery(id+"F0.wireOp",EDGE,"E275.MirrorC"),sQuery(id+"F0.wireOp",EDGE,"E276.MirrorC"),sQuery(id+"F0.wireOp",EDGE,"E277.MirrorC"),sQuery(id+"F0.wireOp",EDGE,"E278.MirrorC"),sQuery(id+"F0.wireOp",EDGE,"E279.MirrorC"),sQuery(id+"F0.wireOp",EDGE,"E280.MirrorC"),sQuery(id+"F0.wireOp",EDGE,"E281.MirrorC"),sQuery(id+"F0.wireOp",EDGE,"E282.MirrorC"),sQuery(id+"F0.wireOp",EDGE,"E283.MirrorC"),sQuery(id+"F0.wireOp",EDGE,"E284.MirrorC"),sQuery(id+"F0.wireOp",EDGE,"E285.MirrorC"),sQuery(id+"F0.wireOp",EDGE,"E286.MirrorC"),sQuery(id+"F0.wireOp",EDGE,"E287.MirrorC"),sQuery(id+"F0.wireOp",EDGE,"E288.MirrorC"),sQuery(id+"F0.wireOp",EDGE,"E289.MirrorC"),sQuery(id+"F0.wireOp",EDGE,"E290.MirrorC"),sQuery(id+"F0.wireOp",EDGE,"E291.MirrorC"),sQuery(id+"F0.wireOp",EDGE,"E292.MirrorC"),sQuery(id+"F0.wireOp",EDGE,"E293.MirrorC"),sQuery(id+"F0.wireOp",EDGE,"E294.MirrorC"),sQuery(id+"F0.wireOp",EDGE,"E295.MirrorC"),sQuery(id+"F0.wireOp",EDGE,"E296.MirrorC"),sQuery(id+"F0.wireOp",EDGE,"E297.MirrorC"),sQuery(id+"F0.wireOp",EDGE,"E298.MirrorC"),sQuery(id+"F0.wireOp",EDGE,"E299.MirrorC"),sQuery(id+"F0.wireOp",EDGE,"E300.MirrorC"),sQuery(id+"F0.wireOp",EDGE,"E301.MirrorC"),sQuery(id+"F0.wireOp",EDGE,"E302.MirrorC"),sQuery(id+"F0.wireOp",EDGE,"E303.MirrorC"),sQuery(id+"F0.wireOp",EDGE,"E304.MirrorC"),sQuery(id+"F0.wireOp",EDGE,"E305.MirrorC"),sQuery(id+"F0.wireOp",EDGE,"E306.MirrorC"),sQuery(id+"F0.wireOp",EDGE,"E307.MirrorC"),sQuery(id+"F0.wireOp",EDGE,"E308.MirrorC"),sQuery(id+"F0.wireOp",EDGE,"E309.MirrorC"),sQuery(id+"F0.wireOp",EDGE,"E310.MirrorC"),sQuery(id+"F0.wireOp",EDGE,"E311.MirrorC"),sQuery(id+"F0.wireOp",EDGE,"E312.MirrorC"),sQuery(id+"F0.wireOp",EDGE,"E313.MirrorC"),sQuery(id+"F0.wireOp",EDGE,"E314.MirrorC"),sQuery(id+"F0.wireOp",EDGE,"E315.MirrorC"),sQuery(id+"F0.wireOp",EDGE,"E316.MirrorC"),sQuery(id+"F0.wireOp",EDGE,"E317.MirrorC"),sQuery(id+"F0.wireOp",EDGE,"E318.MirrorC"),sQuery(id+"F0.wireOp",EDGE,"E319.MirrorC"),sQuery(id+"F0.wireOp",EDGE,"E320.MirrorC"),sQuery(id+"F0.wireOp",EDGE,"E321.MirrorC"),sQuery(id+"F0.wireOp",EDGE,"E322.MirrorC"),sQuery(id+"F0.wireOp",EDGE,"E323.MirrorC"),sQuery(id+"F0.wireOp",EDGE,"E324.MirrorC"),sQuery(id+"F0.wireOp",EDGE,"E325.MirrorC"),sQuery(id+"F0.wireOp",EDGE,"E326.MirrorC"),sQuery(id+"F0.wireOp",EDGE,"E327.MirrorC"),sQuery(id+"F0.wireOp",EDGE,"E328.MirrorC"),sQuery(id+"F0.wireOp",EDGE,"E329.MirrorC"),sQuery(id+"F0.wireOp",EDGE,"E330.MirrorC"),sQuery(id+"F0.wireOp",EDGE,"E331.MirrorC"),sQuery(id+"F0.wireOp",EDGE,"E332.MirrorC"),sQuery(id+"F0.wireOp",EDGE,"E333.MirrorC"),sQuery(id+"F0.wireOp",EDGE,"E334.MirrorC"),sQuery(id+"F0.wireOp",EDGE,"E335.MirrorC"),sQuery(id+"F0.wireOp",EDGE,"E336.MirrorC"),sQuery(id+"F0.wireOp",EDGE,"E337.MirrorC"),sQuery(id+"F0.wireOp",EDGE,"E338.MirrorC"),sQuery(id+"F0.wireOp",EDGE,"E339.MirrorC"),sQuery(id+"F0.wireOp",EDGE,"E340.MirrorC"),sQuery(id+"F0.wireOp",EDGE,"E341.MirrorC"),sQuery(id+"F0.wireOp",EDGE,"E342.MirrorC"),sQuery(id+"F0.wireOp",EDGE,"E343.MirrorC"),sQuery(id+"F0.wireOp",EDGE,"E344.MirrorC"),sQuery(id+"F0.wireOp",EDGE,"E345.MirrorC"),sQuery(id+"F0.wireOp",EDGE,"E346.MirrorC"),sQuery(id+"F0.wireOp",EDGE,"E347.MirrorC"),sQuery(id+"F0.wireOp",EDGE,"E348.MirrorC"),sQuery(id+"F0.wireOp",EDGE,"E349.MirrorC"),sQuery(id+"F0.wireOp",EDGE,"E350.MirrorC"),sQuery(id+"F0.wireOp",EDGE,"E351.MirrorC"),sQuery(id+"F0.wireOp",EDGE,"E352.MirrorC"),sQuery(id+"F0.wireOp",EDGE,"E353.MirrorC"),sQuery(id+"F0.wireOp",EDGE,"E354.MirrorC"),sQuery(id+"F0.wireOp",EDGE,"E355.MirrorC"),sQuery(id+"F0.wireOp",EDGE,"E356.MirrorC"),sQuery(id+"F0.wireOp",EDGE,"E357.MirrorC"),sQuery(id+"F0.wireOp",EDGE,"E358.MirrorC"),sQuery(id+"F0.wireOp",EDGE,"E359.MirrorC"),sQuery(id+"F0.wireOp",EDGE,"E360.MirrorC"),sQuery(id+"F0.wireOp",EDGE,"E361.MirrorC"),sQuery(id+"F0.wireOp",EDGE,"E362.MirrorC"),sQuery(id+"F0.wireOp",EDGE,"E363.MirrorC"),sQuery(id+"F0.wireOp",EDGE,"E364.MirrorC"),sQuery(id+"F0.wireOp",EDGE,"E365.MirrorC"),sQuery(id+"F0.wireOp",EDGE,"E366.MirrorC"),sQuery(id+"F0.wireOp",EDGE,"E367.MirrorC"),sQuery(id+"F0.wireOp",EDGE,"E368.MirrorC"),sQuery(id+"F0.wireOp",EDGE,"E369.MirrorC"),sQuery(id+"F0.wireOp",EDGE,"E370.MirrorC"),sQuery(id+"F0.wireOp",EDGE,"E371.MirrorC"),sQuery(id+"F0.wireOp",EDGE,"E372.MirrorC"),sQuery(id+"F0.wireOp",EDGE,"E373.MirrorC"),sQuery(id+"F0.wireOp",EDGE,"E374.MirrorC"),sQuery(id+"F0.wireOp",EDGE,"E375.MirrorC"),sQuery(id+"F0.wireOp",EDGE,"E376.MirrorC"),sQuery(id+"F0.wireOp",EDGE,"E377.MirrorC"),sQuery(id+"F0.wireOp",EDGE,"E378.MirrorC"),sQuery(id+"F0.wireOp",EDGE,"E379.MirrorC"),sQuery(id+"F0.wireOp",EDGE,"E380.MirrorC"),sQuery(id+"F0.wireOp",EDGE,"E381.MirrorC"),sQuery(id+"F0.wireOp",EDGE,"E382.MirrorC"),sQuery(id+"F0.wireOp",EDGE,"E383.MirrorC"),sQuery(id+"F0.wireOp",EDGE,"E384.MirrorC"),sQuery(id+"F0.wireOp",EDGE,"E385.MirrorC"),sQuery(id+"F0.wireOp",EDGE,"E386.MirrorC"),sQuery(id+"F0.wireOp",EDGE,"E387.MirrorC"),sQuery(id+"F0.wireOp",EDGE,"E388.MirrorC"),sQuery(id+"F0.wireOp",EDGE,"E389.MirrorC"),sQuery(id+"F0.wireOp",EDGE,"E390.MirrorC"),sQuery(id+"F0.wireOp",EDGE,"E391.MirrorC"),sQuery(id+"F0.wireOp",EDGE,"E392.MirrorC"),sQuery(id+"F0.wireOp",EDGE,"E393.MirrorC"),sQuery(id+"F0.wireOp",EDGE,"E394.MirrorC"),sQuery(id+"F0.wireOp",EDGE,"E395.MirrorC"),sQuery(id+"F0.wireOp",EDGE,"E396.MirrorC"),sQuery(id+"F0.wireOp",EDGE,"E397.MirrorC"),sQuery(id+"F0.wireOp",EDGE,"E398.MirrorC"),sQuery(id+"F0.wireOp",EDGE,"E399.MirrorC"),sQuery(id+"F0.wireOp",EDGE,"E400.MirrorC"),sQuery(id+"F0.wireOp",EDGE,"E401.MirrorC"),sQuery(id+"F0.wireOp",EDGE,"E402.MirrorC"),sQuery(id+"F0.wireOp",EDGE,"E403.MirrorC"),sQuery(id+"F0.wireOp",EDGE,"E404.MirrorC"),sQuery(id+"F0.wireOp",EDGE,"E405.MirrorC"),sQuery(id+"F0.wireOp",EDGE,"E406.MirrorC"),sQuery(id+"F0.wireOp",EDGE,"E407.MirrorC"),sQuery(id+"F0.wireOp",EDGE,"E408.MirrorC"),sQuery(id+"F0.wireOp",EDGE,"E409.MirrorC"),sQuery(id+"F0.wireOp",EDGE,"E410.MirrorC")])],"isStart":false});
            var Q1;
            Q1=makeQuery(id+"F1.opExtrude","CAP_FACE",FACE,{"disambiguationData":[OSD([sQuery(id+"F0.wireOp",EDGE,"E0.bottom"),sQuery(id+"F0.wireOp",EDGE,"E0.top"),sQuery(id+"F0.wireOp",EDGE,"E0.left"),sQuery(id+"F0.wireOp",EDGE,"E0.right"),sQuery(id+"F0.wireOp",EDGE,"E3.1.0.0"),sQuery(id+"F0.wireOp",EDGE,"E3.1.1.0"),sQuery(id+"F0.wireOp",EDGE,"E3.1.2.0"),sQuery(id+"F0.wireOp",EDGE,"E3.1.3.0"),sQuery(id+"F0.wireOp",EDGE,"E3.1.4.0"),sQuery(id+"F0.wireOp",EDGE,"E3.1.5.0"),sQuery(id+"F0.wireOp",EDGE,"E3.1.6.0"),sQuery(id+"F0.wireOp",EDGE,"E3.1.7.0"),sQuery(id+"F0.wireOp",EDGE,"E3.1.8.0"),sQuery(id+"F0.wireOp",EDGE,"E3.1.9.0"),sQuery(id+"F0.wireOp",EDGE,"E3.1.10.0"),sQuery(id+"F0.wireOp",EDGE,"E3.2.0.0"),sQuery(id+"F0.wireOp",EDGE,"E3.2.1.0"),sQuery(id+"F0.wireOp",EDGE,"E3.2.2.0"),sQuery(id+"F0.wireOp",EDGE,"E3.2.3.0"),sQuery(id+"F0.wireOp",EDGE,"E3.2.4.0"),sQuery(id+"F0.wireOp",EDGE,"E3.2.5.0"),sQuery(id+"F0.wireOp",EDGE,"E3.2.6.0"),sQuery(id+"F0.wireOp",EDGE,"E3.2.7.0"),sQuery(id+"F0.wireOp",EDGE,"E3.2.8.0"),sQuery(id+"F0.wireOp",EDGE,"E3.2.9.0"),sQuery(id+"F0.wireOp",EDGE,"E3.2.10.0"),sQuery(id+"F0.wireOp",EDGE,"E3.3.0.0"),sQuery(id+"F0.wireOp",EDGE,"E3.3.1.0"),sQuery(id+"F0.wireOp",EDGE,"E3.3.2.0"),sQuery(id+"F0.wireOp",EDGE,"E3.3.3.0"),sQuery(id+"F0.wireOp",EDGE,"E3.3.4.0"),sQuery(id+"F0.wireOp",EDGE,"E3.3.5.0"),sQuery(id+"F0.wireOp",EDGE,"E3.3.6.0"),sQuery(id+"F0.wireOp",EDGE,"E3.3.7.0"),sQuery(id+"F0.wireOp",EDGE,"E3.3.8.0"),sQuery(id+"F0.wireOp",EDGE,"E3.3.9.0"),sQuery(id+"F0.wireOp",EDGE,"E3.3.10.0"),sQuery(id+"F0.wireOp",EDGE,"E3.4.0.0"),sQuery(id+"F0.wireOp",EDGE,"E3.4.1.0"),sQuery(id+"F0.wireOp",EDGE,"E3.4.2.0"),sQuery(id+"F0.wireOp",EDGE,"E3.4.3.0"),sQuery(id+"F0.wireOp",EDGE,"E3.4.4.0"),sQuery(id+"F0.wireOp",EDGE,"E3.4.5.0"),sQuery(id+"F0.wireOp",EDGE,"E3.4.6.0"),sQuery(id+"F0.wireOp",EDGE,"E3.4.7.0"),sQuery(id+"F0.wireOp",EDGE,"E3.4.8.0"),sQuery(id+"F0.wireOp",EDGE,"E3.4.9.0"),sQuery(id+"F0.wireOp",EDGE,"E3.4.10.0"),sQuery(id+"F0.wireOp",EDGE,"E3.5.0.0"),sQuery(id+"F0.wireOp",EDGE,"E3.5.1.0"),sQuery(id+"F0.wireOp",EDGE,"E3.5.2.0"),sQuery(id+"F0.wireOp",EDGE,"E3.5.3.0"),sQuery(id+"F0.wireOp",EDGE,"E3.5.4.0"),sQuery(id+"F0.wireOp",EDGE,"E3.5.5.0"),sQuery(id+"F0.wireOp",EDGE,"E3.5.6.0"),sQuery(id+"F0.wireOp",EDGE,"E3.5.7.0"),sQuery(id+"F0.wireOp",EDGE,"E3.5.8.0"),sQuery(id+"F0.wireOp",EDGE,"E3.5.9.0"),sQuery(id+"F0.wireOp",EDGE,"E3.5.10.0"),sQuery(id+"F0.wireOp",EDGE,"E3.6.0.0"),sQuery(id+"F0.wireOp",EDGE,"E3.6.1.0"),sQuery(id+"F0.wireOp",EDGE,"E3.6.2.0"),sQuery(id+"F0.wireOp",EDGE,"E3.6.3.0"),sQuery(id+"F0.wireOp",EDGE,"E3.6.4.0"),sQuery(id+"F0.wireOp",EDGE,"E3.6.5.0"),sQuery(id+"F0.wireOp",EDGE,"E3.6.6.0"),sQuery(id+"F0.wireOp",EDGE,"E3.6.7.0"),sQuery(id+"F0.wireOp",EDGE,"E3.6.8.0"),sQuery(id+"F0.wireOp",EDGE,"E3.6.9.0"),sQuery(id+"F0.wireOp",EDGE,"E3.6.10.0"),sQuery(id+"F0.wireOp",EDGE,"E3.7.0.0"),sQuery(id+"F0.wireOp",EDGE,"E3.7.1.0"),sQuery(id+"F0.wireOp",EDGE,"E3.7.2.0"),sQuery(id+"F0.wireOp",EDGE,"E3.7.3.0"),sQuery(id+"F0.wireOp",EDGE,"E3.7.4.0"),sQuery(id+"F0.wireOp",EDGE,"E3.7.5.0"),sQuery(id+"F0.wireOp",EDGE,"E3.7.6.0"),sQuery(id+"F0.wireOp",EDGE,"E3.7.7.0"),sQuery(id+"F0.wireOp",EDGE,"E3.7.8.0"),sQuery(id+"F0.wireOp",EDGE,"E3.7.9.0"),sQuery(id+"F0.wireOp",EDGE,"E3.7.10.0"),sQuery(id+"F0.wireOp",EDGE,"E4.0.1.11"),sQuery(id+"F0.wireOp",EDGE,"E4.0.2.11"),sQuery(id+"F0.wireOp",EDGE,"E4.0.3.11"),sQuery(id+"F0.wireOp",EDGE,"E4.0.4.11"),sQuery(id+"F0.wireOp",EDGE,"E4.0.5.11"),sQuery(id+"F0.wireOp",EDGE,"E4.0.6.11"),sQuery(id+"F0.wireOp",EDGE,"E4.0.7.11"),sQuery(id+"F0.wireOp",EDGE,"E5.0.1.12"),sQuery(id+"F0.wireOp",EDGE,"E5.0.1.13"),sQuery(id+"F0.wireOp",EDGE,"E5.0.1.14"),sQuery(id+"F0.wireOp",EDGE,"E5.0.2.12"),sQuery(id+"F0.wireOp",EDGE,"E5.0.2.13"),sQuery(id+"F0.wireOp",EDGE,"E5.0.2.14"),sQuery(id+"F0.wireOp",EDGE,"E5.0.3.12"),sQuery(id+"F0.wireOp",EDGE,"E5.0.3.13"),sQuery(id+"F0.wireOp",EDGE,"E5.0.3.14"),sQuery(id+"F0.wireOp",EDGE,"E5.0.4.12"),sQuery(id+"F0.wireOp",EDGE,"E5.0.4.13"),sQuery(id+"F0.wireOp",EDGE,"E5.0.4.14"),sQuery(id+"F0.wireOp",EDGE,"E5.0.5.12"),sQuery(id+"F0.wireOp",EDGE,"E5.0.5.13"),sQuery(id+"F0.wireOp",EDGE,"E5.0.5.14"),sQuery(id+"F0.wireOp",EDGE,"E5.0.6.12"),sQuery(id+"F0.wireOp",EDGE,"E5.0.6.13"),sQuery(id+"F0.wireOp",EDGE,"E5.0.6.14"),sQuery(id+"F0.wireOp",EDGE,"E5.0.7.12"),sQuery(id+"F0.wireOp",EDGE,"E5.0.7.13"),sQuery(id+"F0.wireOp",EDGE,"E5.0.7.14"),sQuery(id+"F0.wireOp",EDGE,"E6.0.8.0"),sQuery(id+"F0.wireOp",EDGE,"E6.0.8.1"),sQuery(id+"F0.wireOp",EDGE,"E6.0.8.2"),sQuery(id+"F0.wireOp",EDGE,"E6.0.8.3"),sQuery(id+"F0.wireOp",EDGE,"E6.0.8.4"),sQuery(id+"F0.wireOp",EDGE,"E6.0.8.5"),sQuery(id+"F0.wireOp",EDGE,"E6.0.8.6"),sQuery(id+"F0.wireOp",EDGE,"E6.0.8.7"),sQuery(id+"F0.wireOp",EDGE,"E6.0.8.8"),sQuery(id+"F0.wireOp",EDGE,"E6.0.8.9"),sQuery(id+"F0.wireOp",EDGE,"E6.0.8.10"),sQuery(id+"F0.wireOp",EDGE,"E6.0.8.11"),sQuery(id+"F0.wireOp",EDGE,"E6.0.8.12"),sQuery(id+"F0.wireOp",EDGE,"E6.0.8.13"),sQuery(id+"F0.wireOp",EDGE,"E6.0.8.14"),sQuery(id+"F0.wireOp",EDGE,"E6.0.9.0"),sQuery(id+"F0.wireOp",EDGE,"E6.0.9.1"),sQuery(id+"F0.wireOp",EDGE,"E6.0.9.2"),sQuery(id+"F0.wireOp",EDGE,"E6.0.9.3"),sQuery(id+"F0.wireOp",EDGE,"E6.0.9.4"),sQuery(id+"F0.wireOp",EDGE,"E6.0.9.5"),sQuery(id+"F0.wireOp",EDGE,"E6.0.9.6"),sQuery(id+"F0.wireOp",EDGE,"E6.0.9.7"),sQuery(id+"F0.wireOp",EDGE,"E6.0.9.8"),sQuery(id+"F0.wireOp",EDGE,"E6.0.9.9"),sQuery(id+"F0.wireOp",EDGE,"E6.0.9.10"),sQuery(id+"F0.wireOp",EDGE,"E6.0.9.11"),sQuery(id+"F0.wireOp",EDGE,"E6.0.9.12"),sQuery(id+"F0.wireOp",EDGE,"E6.0.9.13"),sQuery(id+"F0.wireOp",EDGE,"E6.0.9.14"),sQuery(id+"F0.wireOp",EDGE,"E3.0.1.0"),sQuery(id+"F0.wireOp",EDGE,"E8.MirrorC"),sQuery(id+"F0.wireOp",EDGE,"E9.MirrorC"),sQuery(id+"F0.wireOp",EDGE,"E10.MirrorC"),sQuery(id+"F0.wireOp",EDGE,"E11.MirrorC"),sQuery(id+"F0.wireOp",EDGE,"E12.MirrorC"),sQuery(id+"F0.wireOp",EDGE,"E13.MirrorC"),sQuery(id+"F0.wireOp",EDGE,"E14.MirrorC"),sQuery(id+"F0.wireOp",EDGE,"E15.MirrorC"),sQuery(id+"F0.wireOp",EDGE,"E16.MirrorC"),sQuery(id+"F0.wireOp",EDGE,"E17.MirrorC"),sQuery(id+"F0.wireOp",EDGE,"E18.MirrorC"),sQuery(id+"F0.wireOp",EDGE,"E19.MirrorC"),sQuery(id+"F0.wireOp",EDGE,"E20.MirrorC"),sQuery(id+"F0.wireOp",EDGE,"E21.MirrorC"),sQuery(id+"F0.wireOp",EDGE,"E22.MirrorC"),sQuery(id+"F0.wireOp",EDGE,"E23.MirrorC"),sQuery(id+"F0.wireOp",EDGE,"E24.MirrorC"),sQuery(id+"F0.wireOp",EDGE,"E25.MirrorC"),sQuery(id+"F0.wireOp",EDGE,"E26.MirrorC"),sQuery(id+"F0.wireOp",EDGE,"E27.MirrorC"),sQuery(id+"F0.wireOp",EDGE,"E28.MirrorC"),sQuery(id+"F0.wireOp",EDGE,"E29.MirrorC"),sQuery(id+"F0.wireOp",EDGE,"E30.MirrorC"),sQuery(id+"F0.wireOp",EDGE,"E31.MirrorC"),sQuery(id+"F0.wireOp",EDGE,"E32.MirrorC"),sQuery(id+"F0.wireOp",EDGE,"E33.MirrorC"),sQuery(id+"F0.wireOp",EDGE,"E4.0.0.11"),sQuery(id+"F0.wireOp",EDGE,"E34.MirrorC"),sQuery(id+"F0.wireOp",EDGE,"E35.MirrorC"),sQuery(id+"F0.wireOp",EDGE,"E3.0.4.0"),sQuery(id+"F0.wireOp",EDGE,"E3.0.6.0"),sQuery(id+"F0.wireOp",EDGE,"E3.0.7.0"),sQuery(id+"F0.wireOp",EDGE,"E36.MirrorC"),sQuery(id+"F0.wireOp",EDGE,"E37.MirrorC"),sQuery(id+"F0.wireOp",EDGE,"E38.MirrorC"),sQuery(id+"F0.wireOp",EDGE,"E39.MirrorC"),sQuery(id+"F0.wireOp",EDGE,"E40.MirrorC"),sQuery(id+"F0.wireOp",EDGE,"E41.MirrorC"),sQuery(id+"F0.wireOp",EDGE,"E42.MirrorC"),sQuery(id+"F0.wireOp",EDGE,"E3.0.3.0"),sQuery(id+"F0.wireOp",EDGE,"E43.MirrorC"),sQuery(id+"F0.wireOp",EDGE,"E44.MirrorC"),sQuery(id+"F0.wireOp",EDGE,"E45.MirrorC"),sQuery(id+"F0.wireOp",EDGE,"E46.MirrorC"),sQuery(id+"F0.wireOp",EDGE,"E47.MirrorC"),sQuery(id+"F0.wireOp",EDGE,"E48.MirrorC"),sQuery(id+"F0.wireOp",EDGE,"E49.MirrorC"),sQuery(id+"F0.wireOp",EDGE,"E50.MirrorC"),sQuery(id+"F0.wireOp",EDGE,"E51.MirrorC"),sQuery(id+"F0.wireOp",EDGE,"E52.MirrorC"),sQuery(id+"F0.wireOp",EDGE,"E53.MirrorC"),sQuery(id+"F0.wireOp",EDGE,"E54.MirrorC"),sQuery(id+"F0.wireOp",EDGE,"E55.MirrorC"),sQuery(id+"F0.wireOp",EDGE,"E56.MirrorC"),sQuery(id+"F0.wireOp",EDGE,"E5.0.0.13"),sQuery(id+"F0.wireOp",EDGE,"E57.MirrorC"),sQuery(id+"F0.wireOp",EDGE,"E58.MirrorC"),sQuery(id+"F0.wireOp",EDGE,"E59.MirrorC"),sQuery(id+"F0.wireOp",EDGE,"E60.MirrorC"),sQuery(id+"F0.wireOp",EDGE,"E61.MirrorC"),sQuery(id+"F0.wireOp",EDGE,"E62.MirrorC"),sQuery(id+"F0.wireOp",EDGE,"E63.MirrorC"),sQuery(id+"F0.wireOp",EDGE,"E64.MirrorC"),sQuery(id+"F0.wireOp",EDGE,"E65.MirrorC"),sQuery(id+"F0.wireOp",EDGE,"E66.MirrorC"),sQuery(id+"F0.wireOp",EDGE,"E67.MirrorC"),sQuery(id+"F0.wireOp",EDGE,"E68.MirrorC"),sQuery(id+"F0.wireOp",EDGE,"E69.MirrorC"),sQuery(id+"F0.wireOp",EDGE,"E70.MirrorC"),sQuery(id+"F0.wireOp",EDGE,"E5.0.0.12"),sQuery(id+"F0.wireOp",EDGE,"E71.MirrorC"),sQuery(id+"F0.wireOp",EDGE,"E72.MirrorC"),sQuery(id+"F0.wireOp",EDGE,"E73.MirrorC"),sQuery(id+"F0.wireOp",EDGE,"E74.MirrorC"),sQuery(id+"F0.wireOp",EDGE,"E75.MirrorC"),sQuery(id+"F0.wireOp",EDGE,"E76.MirrorC"),sQuery(id+"F0.wireOp",EDGE,"E3.0.5.0"),sQuery(id+"F0.wireOp",EDGE,"E77.MirrorC"),sQuery(id+"F0.wireOp",EDGE,"E78.MirrorC"),sQuery(id+"F0.wireOp",EDGE,"E79.MirrorC"),sQuery(id+"F0.wireOp",EDGE,"E80.MirrorC"),sQuery(id+"F0.wireOp",EDGE,"E81.MirrorC"),sQuery(id+"F0.wireOp",EDGE,"E82.MirrorC"),sQuery(id+"F0.wireOp",EDGE,"E83.MirrorC"),sQuery(id+"F0.wireOp",EDGE,"E84.MirrorC"),sQuery(id+"F0.wireOp",EDGE,"E85.MirrorC"),sQuery(id+"F0.wireOp",EDGE,"E86.MirrorC"),sQuery(id+"F0.wireOp",EDGE,"E87.MirrorC"),sQuery(id+"F0.wireOp",EDGE,"E88.MirrorC"),sQuery(id+"F0.wireOp",EDGE,"E89.MirrorC"),sQuery(id+"F0.wireOp",EDGE,"E90.MirrorC"),sQuery(id+"F0.wireOp",EDGE,"E91.MirrorC"),sQuery(id+"F0.wireOp",EDGE,"E92.MirrorC"),sQuery(id+"F0.wireOp",EDGE,"E93.MirrorC"),sQuery(id+"F0.wireOp",EDGE,"E94.MirrorC"),sQuery(id+"F0.wireOp",EDGE,"E95.MirrorC"),sQuery(id+"F0.wireOp",EDGE,"E96.MirrorC"),sQuery(id+"F0.wireOp",EDGE,"E97.MirrorC"),sQuery(id+"F0.wireOp",EDGE,"E98.MirrorC"),sQuery(id+"F0.wireOp",EDGE,"E3.0.2.0"),sQuery(id+"F0.wireOp",EDGE,"E99.MirrorC"),sQuery(id+"F0.wireOp",EDGE,"E100.MirrorC"),sQuery(id+"F0.wireOp",EDGE,"E101.MirrorC"),sQuery(id+"F0.wireOp",EDGE,"E5.0.0.14"),sQuery(id+"F0.wireOp",EDGE,"E102.MirrorC"),sQuery(id+"F0.wireOp",EDGE,"E103.MirrorC"),sQuery(id+"F0.wireOp",EDGE,"E104.MirrorC"),sQuery(id+"F0.wireOp",EDGE,"E105.MirrorC"),sQuery(id+"F0.wireOp",EDGE,"E106.MirrorC"),sQuery(id+"F0.wireOp",EDGE,"E107.MirrorC"),sQuery(id+"F0.wireOp",EDGE,"E108.MirrorC"),sQuery(id+"F0.wireOp",EDGE,"E109.MirrorC"),sQuery(id+"F0.wireOp",EDGE,"E110.MirrorC"),sQuery(id+"F0.wireOp",EDGE,"E111.MirrorC"),sQuery(id+"F0.wireOp",EDGE,"E112.MirrorC"),sQuery(id+"F0.wireOp",EDGE,"E113.MirrorC"),sQuery(id+"F0.wireOp",EDGE,"E114.MirrorC"),sQuery(id+"F0.wireOp",EDGE,"E115.MirrorC"),sQuery(id+"F0.wireOp",EDGE,"E116.MirrorC"),sQuery(id+"F0.wireOp",EDGE,"E117.MirrorC"),sQuery(id+"F0.wireOp",EDGE,"E118.MirrorC"),sQuery(id+"F0.wireOp",EDGE,"E119.MirrorC"),sQuery(id+"F0.wireOp",EDGE,"E120.MirrorC"),sQuery(id+"F0.wireOp",EDGE,"E121.MirrorC"),sQuery(id+"F0.wireOp",EDGE,"E122.MirrorC"),sQuery(id+"F0.wireOp",EDGE,"E123.MirrorC"),sQuery(id+"F0.wireOp",EDGE,"E124.MirrorC"),sQuery(id+"F0.wireOp",EDGE,"E125.MirrorC"),sQuery(id+"F0.wireOp",EDGE,"E126.MirrorC"),sQuery(id+"F0.wireOp",EDGE,"E127.MirrorC"),sQuery(id+"F0.wireOp",EDGE,"E3.0.8.0"),sQuery(id+"F0.wireOp",EDGE,"E3.0.10.0"),sQuery(id+"F0.wireOp",EDGE,"E128.MirrorC"),sQuery(id+"F0.wireOp",EDGE,"E129.MirrorC"),sQuery(id+"F0.wireOp",EDGE,"E3.0.9.0"),sQuery(id+"F0.wireOp",EDGE,"E130.MirrorC"),sQuery(id+"F0.wireOp",EDGE,"E131.MirrorC"),sQuery(id+"F0.wireOp",EDGE,"E132.MirrorC"),sQuery(id+"F0.wireOp",EDGE,"E133.MirrorC"),sQuery(id+"F0.wireOp",EDGE,"E2"),sQuery(id+"F0.wireOp",EDGE,"E135.MirrorC"),sQuery(id+"F0.wireOp",EDGE,"E136.MirrorC"),sQuery(id+"F0.wireOp",EDGE,"E137.MirrorC"),sQuery(id+"F0.wireOp",EDGE,"E138.MirrorC"),sQuery(id+"F0.wireOp",EDGE,"E139.MirrorC"),sQuery(id+"F0.wireOp",EDGE,"E140.MirrorC"),sQuery(id+"F0.wireOp",EDGE,"E141.MirrorC"),sQuery(id+"F0.wireOp",EDGE,"E142.MirrorC"),sQuery(id+"F0.wireOp",EDGE,"E143.MirrorC"),sQuery(id+"F0.wireOp",EDGE,"E145.MirrorC"),sQuery(id+"F0.wireOp",EDGE,"E147.MirrorC"),sQuery(id+"F0.wireOp",EDGE,"E148.MirrorC"),sQuery(id+"F0.wireOp",EDGE,"E158.MirrorC"),sQuery(id+"F0.wireOp",EDGE,"E151.MirrorC"),sQuery(id+"F0.wireOp",EDGE,"E154.MirrorC"),sQuery(id+"F0.wireOp",EDGE,"E155.MirrorC"),sQuery(id+"F0.wireOp",EDGE,"E146.MirrorC"),sQuery(id+"F0.wireOp",EDGE,"E156.MirrorC"),sQuery(id+"F0.wireOp",EDGE,"E152.MirrorC"),sQuery(id+"F0.wireOp",EDGE,"E149.MirrorC"),sQuery(id+"F0.wireOp",EDGE,"E153.MirrorC"),sQuery(id+"F0.wireOp",EDGE,"E150.MirrorC"),sQuery(id+"F0.wireOp",EDGE,"E157.MirrorC"),sQuery(id+"F0.wireOp",EDGE,"E159.MirrorC"),sQuery(id+"F0.wireOp",EDGE,"E160.MirrorC"),sQuery(id+"F0.wireOp",EDGE,"E161.MirrorC"),sQuery(id+"F0.wireOp",EDGE,"E162.MirrorC"),sQuery(id+"F0.wireOp",EDGE,"E163.MirrorC"),sQuery(id+"F0.wireOp",EDGE,"E164.MirrorC"),sQuery(id+"F0.wireOp",EDGE,"E165.MirrorC"),sQuery(id+"F0.wireOp",EDGE,"E166.MirrorC"),sQuery(id+"F0.wireOp",EDGE,"E167.MirrorC"),sQuery(id+"F0.wireOp",EDGE,"E168.MirrorC"),sQuery(id+"F0.wireOp",EDGE,"E169.MirrorC"),sQuery(id+"F0.wireOp",EDGE,"E170.MirrorC"),sQuery(id+"F0.wireOp",EDGE,"E171.MirrorC"),sQuery(id+"F0.wireOp",EDGE,"E172.MirrorC"),sQuery(id+"F0.wireOp",EDGE,"E173.MirrorC"),sQuery(id+"F0.wireOp",EDGE,"E174.MirrorC"),sQuery(id+"F0.wireOp",EDGE,"E175.MirrorC"),sQuery(id+"F0.wireOp",EDGE,"E176.MirrorC"),sQuery(id+"F0.wireOp",EDGE,"E177.MirrorC"),sQuery(id+"F0.wireOp",EDGE,"E178.MirrorC"),sQuery(id+"F0.wireOp",EDGE,"E179.MirrorC"),sQuery(id+"F0.wireOp",EDGE,"E180.MirrorC"),sQuery(id+"F0.wireOp",EDGE,"E181.MirrorC"),sQuery(id+"F0.wireOp",EDGE,"E182.MirrorC"),sQuery(id+"F0.wireOp",EDGE,"E183.MirrorC"),sQuery(id+"F0.wireOp",EDGE,"E184.MirrorC"),sQuery(id+"F0.wireOp",EDGE,"E185.MirrorC"),sQuery(id+"F0.wireOp",EDGE,"E186.MirrorC"),sQuery(id+"F0.wireOp",EDGE,"E187.MirrorC"),sQuery(id+"F0.wireOp",EDGE,"E188.MirrorC"),sQuery(id+"F0.wireOp",EDGE,"E189.MirrorC"),sQuery(id+"F0.wireOp",EDGE,"E190.MirrorC"),sQuery(id+"F0.wireOp",EDGE,"E191.MirrorC"),sQuery(id+"F0.wireOp",EDGE,"E192.MirrorC"),sQuery(id+"F0.wireOp",EDGE,"E193.MirrorC"),sQuery(id+"F0.wireOp",EDGE,"E194.MirrorC"),sQuery(id+"F0.wireOp",EDGE,"E195.MirrorC"),sQuery(id+"F0.wireOp",EDGE,"E196.MirrorC"),sQuery(id+"F0.wireOp",EDGE,"E197.MirrorC"),sQuery(id+"F0.wireOp",EDGE,"E198.MirrorC"),sQuery(id+"F0.wireOp",EDGE,"E199.MirrorC"),sQuery(id+"F0.wireOp",EDGE,"E200.MirrorC"),sQuery(id+"F0.wireOp",EDGE,"E201.MirrorC"),sQuery(id+"F0.wireOp",EDGE,"E202.MirrorC"),sQuery(id+"F0.wireOp",EDGE,"E203.MirrorC"),sQuery(id+"F0.wireOp",EDGE,"E204.MirrorC"),sQuery(id+"F0.wireOp",EDGE,"E205.MirrorC"),sQuery(id+"F0.wireOp",EDGE,"E206.MirrorC"),sQuery(id+"F0.wireOp",EDGE,"E207.MirrorC"),sQuery(id+"F0.wireOp",EDGE,"E208.MirrorC"),sQuery(id+"F0.wireOp",EDGE,"E209.MirrorC"),sQuery(id+"F0.wireOp",EDGE,"E210.MirrorC"),sQuery(id+"F0.wireOp",EDGE,"E211.MirrorC"),sQuery(id+"F0.wireOp",EDGE,"E212.MirrorC"),sQuery(id+"F0.wireOp",EDGE,"E213.MirrorC"),sQuery(id+"F0.wireOp",EDGE,"E214.MirrorC"),sQuery(id+"F0.wireOp",EDGE,"E215.MirrorC"),sQuery(id+"F0.wireOp",EDGE,"E216.MirrorC"),sQuery(id+"F0.wireOp",EDGE,"E217.MirrorC"),sQuery(id+"F0.wireOp",EDGE,"E218.MirrorC"),sQuery(id+"F0.wireOp",EDGE,"E219.MirrorC"),sQuery(id+"F0.wireOp",EDGE,"E220.MirrorC"),sQuery(id+"F0.wireOp",EDGE,"E221.MirrorC"),sQuery(id+"F0.wireOp",EDGE,"E222.MirrorC"),sQuery(id+"F0.wireOp",EDGE,"E223.MirrorC"),sQuery(id+"F0.wireOp",EDGE,"E224.MirrorC"),sQuery(id+"F0.wireOp",EDGE,"E225.MirrorC"),sQuery(id+"F0.wireOp",EDGE,"E226.MirrorC"),sQuery(id+"F0.wireOp",EDGE,"E227.MirrorC"),sQuery(id+"F0.wireOp",EDGE,"E228.MirrorC"),sQuery(id+"F0.wireOp",EDGE,"E229.MirrorC"),sQuery(id+"F0.wireOp",EDGE,"E230.MirrorC"),sQuery(id+"F0.wireOp",EDGE,"E231.MirrorC"),sQuery(id+"F0.wireOp",EDGE,"E232.MirrorC"),sQuery(id+"F0.wireOp",EDGE,"E233.MirrorC"),sQuery(id+"F0.wireOp",EDGE,"E234.MirrorC"),sQuery(id+"F0.wireOp",EDGE,"E235.MirrorC"),sQuery(id+"F0.wireOp",EDGE,"E236.MirrorC"),sQuery(id+"F0.wireOp",EDGE,"E237.MirrorC"),sQuery(id+"F0.wireOp",EDGE,"E238.MirrorC"),sQuery(id+"F0.wireOp",EDGE,"E239.MirrorC"),sQuery(id+"F0.wireOp",EDGE,"E240.MirrorC"),sQuery(id+"F0.wireOp",EDGE,"E241.MirrorC"),sQuery(id+"F0.wireOp",EDGE,"E242.MirrorC"),sQuery(id+"F0.wireOp",EDGE,"E243.MirrorC"),sQuery(id+"F0.wireOp",EDGE,"E244.MirrorC"),sQuery(id+"F0.wireOp",EDGE,"E245.MirrorC"),sQuery(id+"F0.wireOp",EDGE,"E246.MirrorC"),sQuery(id+"F0.wireOp",EDGE,"E247.MirrorC"),sQuery(id+"F0.wireOp",EDGE,"E248.MirrorC"),sQuery(id+"F0.wireOp",EDGE,"E249.MirrorC"),sQuery(id+"F0.wireOp",EDGE,"E250.MirrorC"),sQuery(id+"F0.wireOp",EDGE,"E251.MirrorC"),sQuery(id+"F0.wireOp",EDGE,"E252.MirrorC"),sQuery(id+"F0.wireOp",EDGE,"E253.MirrorC"),sQuery(id+"F0.wireOp",EDGE,"E254.MirrorC"),sQuery(id+"F0.wireOp",EDGE,"E255.MirrorC"),sQuery(id+"F0.wireOp",EDGE,"E256.MirrorC"),sQuery(id+"F0.wireOp",EDGE,"E257.MirrorC"),sQuery(id+"F0.wireOp",EDGE,"E258.MirrorC"),sQuery(id+"F0.wireOp",EDGE,"E259.MirrorC"),sQuery(id+"F0.wireOp",EDGE,"E260.MirrorC"),sQuery(id+"F0.wireOp",EDGE,"E261.MirrorC"),sQuery(id+"F0.wireOp",EDGE,"E262.MirrorC"),sQuery(id+"F0.wireOp",EDGE,"E263.MirrorC"),sQuery(id+"F0.wireOp",EDGE,"E264.MirrorC"),sQuery(id+"F0.wireOp",EDGE,"E265.MirrorC"),sQuery(id+"F0.wireOp",EDGE,"E266.MirrorC"),sQuery(id+"F0.wireOp",EDGE,"E267.MirrorC"),sQuery(id+"F0.wireOp",EDGE,"E268.MirrorC"),sQuery(id+"F0.wireOp",EDGE,"E269.MirrorC"),sQuery(id+"F0.wireOp",EDGE,"E270.MirrorC"),sQuery(id+"F0.wireOp",EDGE,"E271.MirrorC"),sQuery(id+"F0.wireOp",EDGE,"E272.MirrorC"),sQuery(id+"F0.wireOp",EDGE,"E273.MirrorC"),sQuery(id+"F0.wireOp",EDGE,"E274.MirrorC"),sQuery(id+"F0.wireOp",EDGE,"E275.MirrorC"),sQuery(id+"F0.wireOp",EDGE,"E276.MirrorC"),sQuery(id+"F0.wireOp",EDGE,"E277.MirrorC"),sQuery(id+"F0.wireOp",EDGE,"E278.MirrorC"),sQuery(id+"F0.wireOp",EDGE,"E279.MirrorC"),sQuery(id+"F0.wireOp",EDGE,"E280.MirrorC"),sQuery(id+"F0.wireOp",EDGE,"E281.MirrorC"),sQuery(id+"F0.wireOp",EDGE,"E282.MirrorC"),sQuery(id+"F0.wireOp",EDGE,"E283.MirrorC"),sQuery(id+"F0.wireOp",EDGE,"E284.MirrorC"),sQuery(id+"F0.wireOp",EDGE,"E285.MirrorC"),sQuery(id+"F0.wireOp",EDGE,"E286.MirrorC"),sQuery(id+"F0.wireOp",EDGE,"E287.MirrorC"),sQuery(id+"F0.wireOp",EDGE,"E288.MirrorC"),sQuery(id+"F0.wireOp",EDGE,"E289.MirrorC"),sQuery(id+"F0.wireOp",EDGE,"E290.MirrorC"),sQuery(id+"F0.wireOp",EDGE,"E291.MirrorC"),sQuery(id+"F0.wireOp",EDGE,"E292.MirrorC"),sQuery(id+"F0.wireOp",EDGE,"E293.MirrorC"),sQuery(id+"F0.wireOp",EDGE,"E294.MirrorC"),sQuery(id+"F0.wireOp",EDGE,"E295.MirrorC"),sQuery(id+"F0.wireOp",EDGE,"E296.MirrorC"),sQuery(id+"F0.wireOp",EDGE,"E297.MirrorC"),sQuery(id+"F0.wireOp",EDGE,"E298.MirrorC"),sQuery(id+"F0.wireOp",EDGE,"E299.MirrorC"),sQuery(id+"F0.wireOp",EDGE,"E300.MirrorC"),sQuery(id+"F0.wireOp",EDGE,"E301.MirrorC"),sQuery(id+"F0.wireOp",EDGE,"E302.MirrorC"),sQuery(id+"F0.wireOp",EDGE,"E303.MirrorC"),sQuery(id+"F0.wireOp",EDGE,"E304.MirrorC"),sQuery(id+"F0.wireOp",EDGE,"E305.MirrorC"),sQuery(id+"F0.wireOp",EDGE,"E306.MirrorC"),sQuery(id+"F0.wireOp",EDGE,"E307.MirrorC"),sQuery(id+"F0.wireOp",EDGE,"E308.MirrorC"),sQuery(id+"F0.wireOp",EDGE,"E309.MirrorC"),sQuery(id+"F0.wireOp",EDGE,"E310.MirrorC"),sQuery(id+"F0.wireOp",EDGE,"E311.MirrorC"),sQuery(id+"F0.wireOp",EDGE,"E312.MirrorC"),sQuery(id+"F0.wireOp",EDGE,"E313.MirrorC"),sQuery(id+"F0.wireOp",EDGE,"E314.MirrorC"),sQuery(id+"F0.wireOp",EDGE,"E315.MirrorC"),sQuery(id+"F0.wireOp",EDGE,"E316.MirrorC"),sQuery(id+"F0.wireOp",EDGE,"E317.MirrorC"),sQuery(id+"F0.wireOp",EDGE,"E318.MirrorC"),sQuery(id+"F0.wireOp",EDGE,"E319.MirrorC"),sQuery(id+"F0.wireOp",EDGE,"E320.MirrorC"),sQuery(id+"F0.wireOp",EDGE,"E321.MirrorC"),sQuery(id+"F0.wireOp",EDGE,"E322.MirrorC"),sQuery(id+"F0.wireOp",EDGE,"E323.MirrorC"),sQuery(id+"F0.wireOp",EDGE,"E324.MirrorC"),sQuery(id+"F0.wireOp",EDGE,"E325.MirrorC"),sQuery(id+"F0.wireOp",EDGE,"E326.MirrorC"),sQuery(id+"F0.wireOp",EDGE,"E327.MirrorC"),sQuery(id+"F0.wireOp",EDGE,"E328.MirrorC"),sQuery(id+"F0.wireOp",EDGE,"E329.MirrorC"),sQuery(id+"F0.wireOp",EDGE,"E330.MirrorC"),sQuery(id+"F0.wireOp",EDGE,"E331.MirrorC"),sQuery(id+"F0.wireOp",EDGE,"E332.MirrorC"),sQuery(id+"F0.wireOp",EDGE,"E333.MirrorC"),sQuery(id+"F0.wireOp",EDGE,"E334.MirrorC"),sQuery(id+"F0.wireOp",EDGE,"E335.MirrorC"),sQuery(id+"F0.wireOp",EDGE,"E336.MirrorC"),sQuery(id+"F0.wireOp",EDGE,"E337.MirrorC"),sQuery(id+"F0.wireOp",EDGE,"E338.MirrorC"),sQuery(id+"F0.wireOp",EDGE,"E339.MirrorC"),sQuery(id+"F0.wireOp",EDGE,"E340.MirrorC"),sQuery(id+"F0.wireOp",EDGE,"E341.MirrorC"),sQuery(id+"F0.wireOp",EDGE,"E342.MirrorC"),sQuery(id+"F0.wireOp",EDGE,"E343.MirrorC"),sQuery(id+"F0.wireOp",EDGE,"E344.MirrorC"),sQuery(id+"F0.wireOp",EDGE,"E345.MirrorC"),sQuery(id+"F0.wireOp",EDGE,"E346.MirrorC"),sQuery(id+"F0.wireOp",EDGE,"E347.MirrorC"),sQuery(id+"F0.wireOp",EDGE,"E348.MirrorC"),sQuery(id+"F0.wireOp",EDGE,"E349.MirrorC"),sQuery(id+"F0.wireOp",EDGE,"E350.MirrorC"),sQuery(id+"F0.wireOp",EDGE,"E351.MirrorC"),sQuery(id+"F0.wireOp",EDGE,"E352.MirrorC"),sQuery(id+"F0.wireOp",EDGE,"E353.MirrorC"),sQuery(id+"F0.wireOp",EDGE,"E354.MirrorC"),sQuery(id+"F0.wireOp",EDGE,"E355.MirrorC"),sQuery(id+"F0.wireOp",EDGE,"E356.MirrorC"),sQuery(id+"F0.wireOp",EDGE,"E357.MirrorC"),sQuery(id+"F0.wireOp",EDGE,"E358.MirrorC"),sQuery(id+"F0.wireOp",EDGE,"E359.MirrorC"),sQuery(id+"F0.wireOp",EDGE,"E360.MirrorC"),sQuery(id+"F0.wireOp",EDGE,"E361.MirrorC"),sQuery(id+"F0.wireOp",EDGE,"E362.MirrorC"),sQuery(id+"F0.wireOp",EDGE,"E363.MirrorC"),sQuery(id+"F0.wireOp",EDGE,"E364.MirrorC"),sQuery(id+"F0.wireOp",EDGE,"E365.MirrorC"),sQuery(id+"F0.wireOp",EDGE,"E366.MirrorC"),sQuery(id+"F0.wireOp",EDGE,"E367.MirrorC"),sQuery(id+"F0.wireOp",EDGE,"E368.MirrorC"),sQuery(id+"F0.wireOp",EDGE,"E369.MirrorC"),sQuery(id+"F0.wireOp",EDGE,"E370.MirrorC"),sQuery(id+"F0.wireOp",EDGE,"E371.MirrorC"),sQuery(id+"F0.wireOp",EDGE,"E372.MirrorC"),sQuery(id+"F0.wireOp",EDGE,"E373.MirrorC"),sQuery(id+"F0.wireOp",EDGE,"E374.MirrorC"),sQuery(id+"F0.wireOp",EDGE,"E375.MirrorC"),sQuery(id+"F0.wireOp",EDGE,"E376.MirrorC"),sQuery(id+"F0.wireOp",EDGE,"E377.MirrorC"),sQuery(id+"F0.wireOp",EDGE,"E378.MirrorC"),sQuery(id+"F0.wireOp",EDGE,"E379.MirrorC"),sQuery(id+"F0.wireOp",EDGE,"E380.MirrorC"),sQuery(id+"F0.wireOp",EDGE,"E381.MirrorC"),sQuery(id+"F0.wireOp",EDGE,"E382.MirrorC"),sQuery(id+"F0.wireOp",EDGE,"E383.MirrorC"),sQuery(id+"F0.wireOp",EDGE,"E384.MirrorC"),sQuery(id+"F0.wireOp",EDGE,"E385.MirrorC"),sQuery(id+"F0.wireOp",EDGE,"E386.MirrorC"),sQuery(id+"F0.wireOp",EDGE,"E387.MirrorC"),sQuery(id+"F0.wireOp",EDGE,"E388.MirrorC"),sQuery(id+"F0.wireOp",EDGE,"E389.MirrorC"),sQuery(id+"F0.wireOp",EDGE,"E390.MirrorC"),sQuery(id+"F0.wireOp",EDGE,"E391.MirrorC"),sQuery(id+"F0.wireOp",EDGE,"E392.MirrorC"),sQuery(id+"F0.wireOp",EDGE,"E393.MirrorC"),sQuery(id+"F0.wireOp",EDGE,"E394.MirrorC"),sQuery(id+"F0.wireOp",EDGE,"E395.MirrorC"),sQuery(id+"F0.wireOp",EDGE,"E396.MirrorC"),sQuery(id+"F0.wireOp",EDGE,"E397.MirrorC"),sQuery(id+"F0.wireOp",EDGE,"E398.MirrorC"),sQuery(id+"F0.wireOp",EDGE,"E399.MirrorC"),sQuery(id+"F0.wireOp",EDGE,"E400.MirrorC"),sQuery(id+"F0.wireOp",EDGE,"E401.MirrorC"),sQuery(id+"F0.wireOp",EDGE,"E402.MirrorC"),sQuery(id+"F0.wireOp",EDGE,"E403.MirrorC"),sQuery(id+"F0.wireOp",EDGE,"E404.MirrorC"),sQuery(id+"F0.wireOp",EDGE,"E405.MirrorC"),sQuery(id+"F0.wireOp",EDGE,"E406.MirrorC"),sQuery(id+"F0.wireOp",EDGE,"E407.MirrorC"),sQuery(id+"F0.wireOp",EDGE,"E408.MirrorC"),sQuery(id+"F0.wireOp",EDGE,"E409.MirrorC"),sQuery(id+"F0.wireOp",EDGE,"E410.MirrorC")])],"isStart":true});
            chamfer(context, id + "F2", {"entities" : qUnion([Q0, Q1]), "width" : 0.5 * mm, "tangentPropagation" : true});
        }
    });
